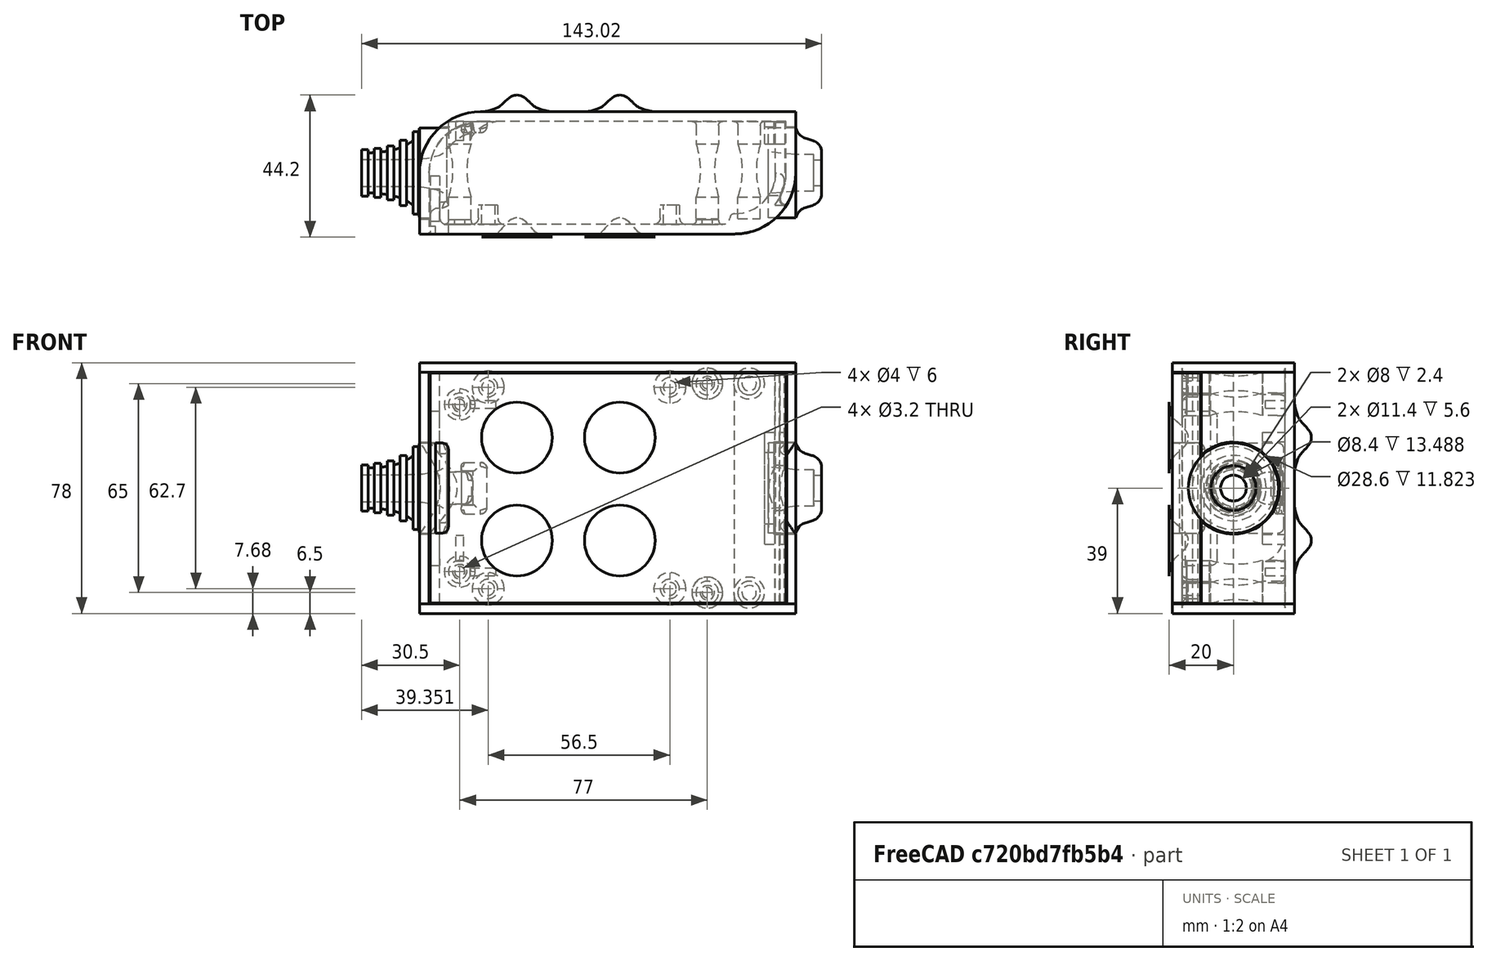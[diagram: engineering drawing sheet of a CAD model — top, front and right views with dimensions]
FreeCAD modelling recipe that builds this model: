
FCSTD DOCUMENT  (FreeCAD 0.19R0.19.2)
Label: enclosure_072
License: All rights reserved
LicenseURL: http://en.wikipedia.org/wiki/All_rights_reserved
objects: Part::MultiFuse×44, Part::Feature×44, Part::Revolution×44, Part::Fillet×22, Part::Cylinder×22, Sketcher::SketchObject×20, Part::Cut×14, Part::Extrusion×13, Part::Box×10, App::MeasureDistance×3
note: 233 computed .brp shape members not serialized (recipe doc carries the construction recipe); baked Part::Feature solids carry a one-line shape summary decoded from their .brp

FEATURE [Sketcher::SketchObject] Sketch  label="topSketch"
  FullyConstrained = true
  sketch-geometry (13):
    g0: LineSegment StartX=117 StartY=19 StartZ=0 EndX=117 EndY=38 EndZ=0
    g1: ArcOfCircle CenterX=98 CenterY=19 CenterZ=0 NormalX=0 NormalY=0 NormalZ=1 AngleXU=0 Radius=19 StartAngle=5.7297 EndAngle=6.28319
    g2: LineSegment StartX=0 StartY=3 StartZ=0 EndX=0 EndY=19 EndZ=0
    g3: LineSegment StartX=19 StartY=38 StartZ=0 EndX=117 EndY=38 EndZ=0
    g4: ArcOfCircle CenterX=19 CenterY=19 CenterZ=0 NormalX=0 NormalY=0 NormalZ=1 AngleXU=0 Radius=19 StartAngle=1.5708 EndAngle=3.14159
    g5: ArcOfCircle CenterX=19 CenterY=19 CenterZ=0 NormalX=0 NormalY=0 NormalZ=1 AngleXU=0 Radius=16 StartAngle=1.5708 EndAngle=3.14159
    g6: ArcOfCircle CenterX=98 CenterY=19 CenterZ=0 NormalX=0 NormalY=0 NormalZ=1 AngleXU=0 Radius=16 StartAngle=5.60905 EndAngle=6.28319
    g7: LineSegment StartX=114 StartY=19 StartZ=0 EndX=114 EndY=35 EndZ=0
    g8: LineSegment StartX=110.5 StartY=9.01251 StartZ=0 EndX=114.163 EndY=9.01251 EndZ=0
    g9: LineSegment StartX=114 StartY=35 StartZ=0 EndX=19 EndY=35 EndZ=0
    g10: LineSegment StartX=0 StartY=3 StartZ=0 EndX=0 EndY=0 EndZ=0
    g11: LineSegment StartX=3 StartY=0 StartZ=0 EndX=0 EndY=0 EndZ=0
    g12: LineSegment StartX=3 StartY=19 StartZ=0 EndX=3 EndY=0 EndZ=0
  constraints (33):
    c: Vertical(g0)
    c: Distance(g0) = 19
    c: Block(g0)
    c: Coincident(g1,g0)
    c: Block(g1)
    c: Vertical(g2)
    c: Block(g2)
    c: Coincident(g3,g0)
    c: Horizontal(g3)
    c: Distance(g3) = 98
    c: Coincident(g4,g3)
    c: Coincident(g4,g2)
    c: Block(g4)
    c: Coincident(g5,g4)
    c: Coincident(g6,g1)
    c: Block(g6)
    c: Block(g5)
    c: Coincident(g7,g6)
    c: Vertical(g7)
    c: Coincident(g8,g6)
    c: Coincident(g8,g1)
    c: Coincident(g9,g7)
    c: Coincident(g9,g5)
    c: Horizontal(g9)
    c: Tangent(g9,g5)
    c: Coincident(g10,g2)
    c: Distance(g10) = 3
    c: Vertical(g10)
    c: Coincident(g11,g10)
    c: Horizontal(g11)
    c: Coincident(g12,g5)
    c: Coincident(g12,g11)
    c: Vertical(g12)
FEATURE [Sketcher::SketchObject] Sketch001  label="bottomSketch"
  FullyConstrained = true
  sketch-geometry (32):
    g0: LineSegment StartX=3.3 StartY=-6.03275e-07 StartZ=0 EndX=98 EndY=-6.03275e-07 EndZ=0
    g1: ArcOfCircle CenterX=98 CenterY=19 CenterZ=0 NormalX=0 NormalY=0 NormalZ=1 AngleXU=0 Radius=19 StartAngle=4.71239 EndAngle=5.71103
    g2: LineSegment StartX=6.3 StartY=8 StartZ=0 EndX=3.3 EndY=8 EndZ=0
    g3: LineSegment StartX=3.3 StartY=8 StartZ=0 EndX=3.3 EndY=-6.03275e-07 EndZ=0
    g4: ArcOfCircle CenterX=8.3 CenterY=5 CenterZ=0 NormalX=0 NormalY=0 NormalZ=1 AngleXU=0 Radius=2 StartAngle=3.14159 EndAngle=4.71239
    g5: LineSegment StartX=6.3 StartY=8 StartZ=0 EndX=6.3 EndY=5 EndZ=0
    g6: ArcOfCircle CenterX=98 CenterY=19 CenterZ=0 NormalX=0 NormalY=0 NormalZ=1 AngleXU=0 Radius=12.7 StartAngle=4.71239 EndAngle=6.28319
    g7: LineSegment StartX=94.7 StartY=3 StartZ=0 EndX=8.3 EndY=3 EndZ=0
    g8-g12: Circle x5 (B-spline internal-alignment scaffolding for g13; pole/knot coordinates omitted)
    g13: BSplineCurve PolesCount=5 KnotsCount=3 Degree=3 IsPeriodic=0
    g14: GeomPoint X=98 Y=6.3 Z=0
    g15: GeomPoint X=96.3938 Y=4.71946 Z=0
    g16: GeomPoint X=94.7 Y=3 Z=0
    g17-g23: Circle x7 (B-spline internal-alignment scaffolding for g24; pole/knot coordinates omitted)
    g24: BSplineCurve PolesCount=7 KnotsCount=5 Degree=3 IsPeriodic=0
    g25-g29: GeomPoint x5 (B-spline internal-alignment scaffolding for g24; pole/knot coordinates omitted)
    g30: ArcOfCircle CenterX=98 CenterY=19 CenterZ=0 NormalX=0 NormalY=0 NormalZ=1 AngleXU=0 Radius=15.7 StartAngle=5.81226 EndAngle=6.28319
    g31: LineSegment StartX=110.7 StartY=19 StartZ=0 EndX=113.7 EndY=19 EndZ=0
  constraints (41):
    c: Horizontal(g0)
    c: Coincident(g1,g0)
    c: Block(g1)
    c: Horizontal(g2)
    c: Distance(g2) = 3
    c: Coincident(g3,g2)
    c: Vertical(g3)
    c: Coincident(g3,g0)
    c: Block(g4)
    c: Block(g2)
    c: Coincident(g5,g2)
    c: Coincident(g5,g4)
    c: Vertical(g5)
    c: Coincident(g6,g1)
    c: Block(g6)
    c: Coincident(g7,g4)
    c: Horizontal(g7)
    c: Block(g0)
    c: Block(g7)
    c: Block(g3)
    c: Coincident(g13,g6)
    c: Weight(g8) = 1
    c: Equal(g8, g9-g12) x4
    c: Coincident(g13,g7)
    c: InternalAlignment(g8-g12 -> g13) x5
    c: InternalAlignment(g14,g13)
    c: InternalAlignment(g15,g13)
    c: InternalAlignment(g16,g13)
    c: Block(g13)
    c: Weight(g17) = 1
    c: Equal(g17, g18-g23) x6
    c: Coincident(g24,g1)
    c: InternalAlignment(g17-g23 -> g24) x7
    c: InternalAlignment(g25-g29 -> g24) x5
    c: Block(g24)
    c: Coincident(g30,g24)
    c: Coincident(g31,g6)
    c: Coincident(g31,g30)
    c: Horizontal(g31)
    c: Block(g31)
    c: Block(g30)
FEATURE [Part::Extrusion] Extrude  label="top"
  Base = -> Sketch
  Dir = (0,0,1)
  DirMode = 2
  FaceMakerClass = Part::FaceMakerBullseye
  LengthFwd = 72
  LengthRev = 0
  Solid = true
  Symmetric = false
FEATURE [Part::Extrusion] Extrude001  label="bottom"
  Base = -> Sketch001
  Dir = (0,0,1)
  DirMode = 2
  FaceMakerClass = Part::FaceMakerBullseye
  LengthFwd = 71.4
  LengthRev = 0
  Placement = pos=(0,0,0.3) rot=(0,0,1;0rad)
  Solid = true
  Symmetric = false
FEATURE [Sketcher::SketchObject] Sketch002  label="topSketch001"
  FullyConstrained = true
  sketch-geometry (6):
    g0: LineSegment StartX=19 StartY=38 StartZ=0 EndX=117 EndY=38 EndZ=0
    g1: ArcOfCircle CenterX=19 CenterY=19 CenterZ=0 NormalX=0 NormalY=0 NormalZ=1 AngleXU=0 Radius=19 StartAngle=1.5708 EndAngle=3.14159
    g2: LineSegment StartX=117 StartY=38 StartZ=0 EndX=117 EndY=19 EndZ=0
    g3: LineSegment StartX=98 StartY=1.0161e-12 StartZ=0 EndX=5.22862e-06 EndY=1.0161e-12 EndZ=0
    g4: LineSegment StartX=5.22862e-06 StartY=19 StartZ=0 EndX=5.22862e-06 EndY=1.0161e-12 EndZ=0
    g5: ArcOfCircle CenterX=98 CenterY=19 CenterZ=0 NormalX=0 NormalY=0 NormalZ=1 AngleXU=0 Radius=19 StartAngle=4.71239 EndAngle=6.28319
  constraints (16):
    c: Horizontal(g0)
    c: Distance(g0) = 98
    c: Coincident(g1,g0)
    c: Block(g1)
    c: Coincident(g2,g0)
    c: Vertical(g2)
    c: Distance(g2) = 19
    c: Horizontal(g3)
    c: Coincident(g4,g1)
    c: Vertical(g4)
    c: Coincident(g3,g4)
    c: Block(g3)
    c: Coincident(g5,g2)
    c: Coincident(g5,g3)
    c: Block(g0)
    c: Block(g5)
FEATURE [Part::Extrusion] Extrude002  label="sideA"
  Base = -> Sketch002
  Dir = (0,0,1)
  DirMode = 2
  FaceMakerClass = Part::FaceMakerBullseye
  LengthFwd = 3
  LengthRev = 0
  Placement = pos=(0,0,-3) rot=(0,0,1;0rad)
  Solid = true
  Symmetric = false
FEATURE [Sketcher::SketchObject] Sketch003  label="topSketch002"
  FullyConstrained = true
  sketch-geometry (6):
    g0: LineSegment StartX=19 StartY=38 StartZ=0 EndX=117 EndY=38 EndZ=0
    g1: ArcOfCircle CenterX=19 CenterY=19 CenterZ=0 NormalX=0 NormalY=0 NormalZ=1 AngleXU=0 Radius=19 StartAngle=1.5708 EndAngle=3.14159
    g2: LineSegment StartX=117 StartY=38 StartZ=0 EndX=117 EndY=19 EndZ=0
    g3: LineSegment StartX=98 StartY=1.0161e-12 StartZ=0 EndX=5.22862e-06 EndY=1.0161e-12 EndZ=0
    g4: LineSegment StartX=5.22862e-06 StartY=19 StartZ=0 EndX=5.22862e-06 EndY=1.0161e-12 EndZ=0
    g5: ArcOfCircle CenterX=98 CenterY=19 CenterZ=0 NormalX=0 NormalY=0 NormalZ=1 AngleXU=0 Radius=19 StartAngle=4.71239 EndAngle=6.28319
  constraints (16):
    c: Horizontal(g0)
    c: Distance(g0) = 98
    c: Coincident(g1,g0)
    c: Block(g1)
    c: Coincident(g2,g0)
    c: Vertical(g2)
    c: Distance(g2) = 19
    c: Horizontal(g3)
    c: Coincident(g4,g1)
    c: Vertical(g4)
    c: Coincident(g3,g4)
    c: Block(g3)
    c: Coincident(g5,g2)
    c: Coincident(g5,g3)
    c: Block(g0)
    c: Block(g5)
FEATURE [Part::Extrusion] Extrude003  label="sideB"
  Base = -> Sketch003
  Dir = (0,0,1)
  DirMode = 2
  FaceMakerClass = Part::FaceMakerBullseye
  LengthFwd = 3
  LengthRev = 0
  Placement = pos=(0,0,72) rot=(0,0,1;0rad)
  Solid = true
  Symmetric = false
FEATURE [Sketcher::SketchObject] Sketch004
  FullyConstrained = true
  MapMode = 3
  Placement = pos=(0,0,0) rot=(1,0,0;1.5708rad)
  Support = -> [Extrude]
  sketch-geometry (8):
    g0: Circle CenterX=80.351 CenterY=-67.6202 CenterZ=0 NormalX=0 NormalY=0 NormalZ=1 AngleXU=0 Radius=2
    g1: Circle CenterX=80.351 CenterY=-67.6202 CenterZ=0 NormalX=0 NormalY=0 NormalZ=1 AngleXU=0 Radius=3
    g2: Circle CenterX=80.351 CenterY=-4.92017 CenterZ=0 NormalX=0 NormalY=0 NormalZ=1 AngleXU=0 Radius=2
    g3: Circle CenterX=80.351 CenterY=-4.92017 CenterZ=0 NormalX=0 NormalY=0 NormalZ=1 AngleXU=0 Radius=3
    g4: Circle CenterX=23.851 CenterY=-4.92017 CenterZ=0 NormalX=0 NormalY=0 NormalZ=1 AngleXU=0 Radius=2
    g5: Circle CenterX=23.851 CenterY=-4.92017 CenterZ=0 NormalX=0 NormalY=0 NormalZ=1 AngleXU=0 Radius=3
    g6: Circle CenterX=23.851 CenterY=-67.6202 CenterZ=0 NormalX=0 NormalY=0 NormalZ=1 AngleXU=0 Radius=2
    g7: Circle CenterX=23.851 CenterY=-67.6202 CenterZ=0 NormalX=0 NormalY=0 NormalZ=1 AngleXU=0 Radius=3
  constraints (8):
    c: Block(g3)
    c: Block(g2)
    c: Block(g1)
    c: Block(g0)
    c: Block(g6)
    c: Block(g7)
    c: Block(g4)
    c: Block(g5)
FEATURE [Part::Extrusion] Extrude004
  Base = -> Sketch004
  Dir = (0,-1,2e-16)
  DirMode = 2
  FaceMakerClass = Part::FaceMakerBullseye
  LengthFwd = 6
  LengthRev = 0
  Placement = pos=(0,9,0) rot=(0,0,1;0rad)
  Solid = true
  Symmetric = false
FEATURE [Sketcher::SketchObject] Sketch005
  FullyConstrained = true
  MapMode = 3
  Placement = pos=(0,0,0) rot=(1,0,0;1.5708rad)
  Support = -> [Extrude]
  sketch-geometry (8):
    g0: Circle CenterX=80.351 CenterY=-67.6202 CenterZ=0 NormalX=0 NormalY=0 NormalZ=1 AngleXU=0 Radius=3
    g1: Circle CenterX=80.351 CenterY=-4.92017 CenterZ=0 NormalX=0 NormalY=0 NormalZ=1 AngleXU=0 Radius=3
    g2: Circle CenterX=23.851 CenterY=-4.92017 CenterZ=0 NormalX=0 NormalY=0 NormalZ=1 AngleXU=0 Radius=3
    g3: Circle CenterX=23.851 CenterY=-67.6202 CenterZ=0 NormalX=0 NormalY=0 NormalZ=1 AngleXU=0 Radius=3
    g4: Circle CenterX=23.851 CenterY=-67.6202 CenterZ=0 NormalX=0 NormalY=0 NormalZ=1 AngleXU=0 Radius=5
    g5: Circle CenterX=80.351 CenterY=-67.6202 CenterZ=0 NormalX=0 NormalY=0 NormalZ=1 AngleXU=0 Radius=5
    g6: Circle CenterX=23.851 CenterY=-4.92017 CenterZ=0 NormalX=0 NormalY=0 NormalZ=1 AngleXU=0 Radius=5
    g7: Circle CenterX=80.351 CenterY=-4.92017 CenterZ=0 NormalX=0 NormalY=0 NormalZ=1 AngleXU=0 Radius=5
  constraints (8):
    c: Block(g1)
    c: Block(g0)
    c: Block(g3)
    c: Block(g2)
    c: Block(g5)
    c: Block(g4)
    c: Block(g6)
    c: Block(g7)
FEATURE [Part::Extrusion] Extrude005
  Base = -> Sketch005
  Dir = (0,-1,2e-16)
  DirMode = 2
  FaceMakerClass = Part::FaceMakerBullseye
  LengthFwd = 2
  LengthRev = 0
  Solid = true
  Symmetric = false
FEATURE [Sketcher::SketchObject] Sketch006
  FullyConstrained = true
  MapMode = 3
  Placement = pos=(0,0,0) rot=(1,0,0;1.5708rad)
  sketch-geometry (8):
    g0: Circle CenterX=80.351 CenterY=-67.6202 CenterZ=0 NormalX=0 NormalY=0 NormalZ=1 AngleXU=0 Radius=3
    g1: Circle CenterX=80.351 CenterY=-4.92017 CenterZ=0 NormalX=0 NormalY=0 NormalZ=1 AngleXU=0 Radius=3
    g2: Circle CenterX=23.851 CenterY=-4.92017 CenterZ=0 NormalX=0 NormalY=0 NormalZ=1 AngleXU=0 Radius=3
    g3: Circle CenterX=23.851 CenterY=-67.6202 CenterZ=0 NormalX=0 NormalY=0 NormalZ=1 AngleXU=0 Radius=3
    g4: Circle CenterX=23.851 CenterY=-67.6202 CenterZ=0 NormalX=0 NormalY=0 NormalZ=1 AngleXU=0 Radius=5
    g5: Circle CenterX=80.351 CenterY=-67.6202 CenterZ=0 NormalX=0 NormalY=0 NormalZ=1 AngleXU=0 Radius=5
    g6: Circle CenterX=23.851 CenterY=-4.92017 CenterZ=0 NormalX=0 NormalY=0 NormalZ=1 AngleXU=0 Radius=5
    g7: Circle CenterX=80.351 CenterY=-4.92017 CenterZ=0 NormalX=0 NormalY=0 NormalZ=1 AngleXU=0 Radius=5
  constraints (8):
    c: Block(g1)
    c: Block(g0)
    c: Block(g3)
    c: Block(g2)
    c: Block(g5)
    c: Block(g4)
    c: Block(g6)
    c: Block(g7)
FEATURE [Part::Extrusion] Extrude007
  Base = -> Sketch006
  Dir = (0,-1,2e-16)
  DirMode = 2
  FaceMakerClass = Part::FaceMakerBullseye
  LengthFwd = 2
  LengthRev = 0
  Solid = true
  Symmetric = false
FEATURE [Part::Fillet] Fillet
  Base = -> Extrude007
  Edges = 4 edges r=1.99: [Edge6,Edge12,Edge18,Edge24]
FEATURE [Part::Cut] Cut
  Base = -> Extrude005
  Placement = pos=(0,5,0) rot=(0,0,1;0rad)
  Tool = -> Fillet
FEATURE [Part::MultiFuse] Fusion  label="pCBScrews"
  Placement = pos=(-2.5,0,72.3) rot=(0,0,1;0rad)
  Shapes = -> [Extrude004,Cut]
FEATURE [App::MeasureDistance] Distance  label="Distance: 0.69 mm"
  Distance = 0.685967
  P1 = (24.0138,2.9647,0.3)
  P2 = (23.8901,3,-0.373787)
FEATURE [App::MeasureDistance] Distance001  label="Distance: 0.53 mm"
  Distance = 0.533607
  P1 = (80.2939,3,72.2334)
  P2 = (80.281,2.99661,71.7)
FEATURE [Part::Fillet] Fillet001
  Base = -> Extrude001
  Edges = 1 edges r=2.4: [Edge17]
FEATURE [Part::Fillet] Fillet002  label="bottom001"
  Base = -> Fillet001
  Edges = 1 edges r=2.4: [Edge36]
FEATURE [Part::Fillet] Fillet003  label="top001"
  Base = -> Extrude
  Edges = 1 edges r=2: [Edge1]
FEATURE [Sketcher::SketchObject] Sketch007
  FullyConstrained = true
  sketch-geometry (16):
    g0: LineSegment StartX=4 StartY=0 StartZ=0 EndX=4 EndY=2.4 EndZ=0
    g1: LineSegment StartX=4 StartY=2.4 StartZ=0 EndX=7 EndY=2.4 EndZ=0
    g2: LineSegment StartX=4 StartY=0 StartZ=0 EndX=5.7 EndY=0 EndZ=0
    g3: LineSegment StartX=5.7 StartY=0 StartZ=0 EndX=5.7 EndY=-5.6 EndZ=0
    g4-g8: Circle x5 (B-spline internal-alignment scaffolding for g9; pole/knot coordinates omitted)
    g9: BSplineCurve PolesCount=5 KnotsCount=3 Degree=3 IsPeriodic=0
    g10: GeomPoint X=7 Y=2.4 Z=0
    g11: GeomPoint X=10.4582 Y=-1.55472 Z=0
    g12: GeomPoint X=14 Y=-5.6 Z=0
    g13: LineSegment StartX=14 StartY=-5.6 StartZ=0 EndX=14 EndY=-14.1 EndZ=0
    g14: LineSegment StartX=14 StartY=-14.1 StartZ=0 EndX=6.5 EndY=-14.1 EndZ=0
    g15: LineSegment StartX=5.7 StartY=-5.6 StartZ=0 EndX=6.5 EndY=-14.1 EndZ=0
  constraints (28):
    c: Distance(g0) = 2.4
    c: Vertical(g0)
    c: Block(g0)
    c: Coincident(g1,g0)
    c: Horizontal(g1)
    c: Distance(g1) = 3
    c: Coincident(g2,g0)
    c: Horizontal(g2)
    c: Distance(g2) = 1.7
    c: Coincident(g3,g2)
    c: Vertical(g3)
    c: Distance(g3) = 5.6
    c: Coincident(g9,g1)
    c: Weight(g4) = 1
    c: Equal(g4, g5-g8) x4
    c: InternalAlignment(g4-g8 -> g9) x5
    c: InternalAlignment(g10,g9)
    c: InternalAlignment(g11,g9)
    c: InternalAlignment(g12,g9)
    c: Block(g9)
    c: Coincident(g13,g9)
    c: Vertical(g13)
    c: Distance(g13) = 8.5
    c: Coincident(g14,g13)
    c: Horizontal(g14)
    c: Distance(g14) = 7.5
    c: Coincident(g15,g3)
    c: Coincident(g15,g14)
FEATURE [Part::Feature] Face
  shape: bbox 10 x 16.5 x 2e-07 mm, 1 faces, 0 solids (baked)
FEATURE [Part::Revolution] Revolve  label="plugHousing"
  Angle = 360
  Axis = (0,1,0)
  Base = (0,0,0)
  FaceMakerClass = Part::FaceMakerBullseye
  Placement = pos=(0,0,36.15) rot=(0,0,1;0rad)
  Solid = false
  Source = -> Face
  Symmetric = false
FEATURE [Part::Feature] Face001
  shape: bbox 10 x 16.5 x 2e-07 mm, 1 faces, 0 solids (baked)
FEATURE [Part::Revolution] Revolve001  label="plugHousing001"
  Angle = 360
  Axis = (0,1,0)
  Base = (0,0,0)
  FaceMakerClass = Part::FaceMakerBullseye
  Placement = pos=(0,0,36.15) rot=(0,0,1;0rad)
  Solid = false
  Source = -> Face001
  Symmetric = false
FEATURE [Part::MultiFuse] Fusion001  label="plugHousing002"
  Placement = pos=(0,0,0) rot=(0,0,1;1.5708rad)
  Shapes = -> [Revolve001,Revolve]
FEATURE [Part::Feature] Face002
  shape: bbox 10 x 16.5 x 2e-07 mm, 1 faces, 0 solids (baked)
FEATURE [Part::Revolution] Revolve003  label="plugHousing005"
  Angle = 360
  Axis = (0,1,0)
  Base = (0,0,0)
  FaceMakerClass = Part::FaceMakerBullseye
  Placement = pos=(0,0,36.15) rot=(0,0,1;0rad)
  Solid = false
  Source = -> Face002
  Symmetric = false
FEATURE [Part::Feature] Face003
  shape: bbox 10 x 16.5 x 2e-07 mm, 1 faces, 0 solids (baked)
FEATURE [Part::Revolution] Revolve002  label="plugHousing003"
  Angle = 360
  Axis = (0,1,0)
  Base = (0,0,0)
  FaceMakerClass = Part::FaceMakerBullseye
  Placement = pos=(0,0,36.15) rot=(0,0,1;0rad)
  Solid = false
  Source = -> Face003
  Symmetric = false
FEATURE [Part::MultiFuse] Fusion002  label="plugHousing004"
  Placement = pos=(0,0,0) rot=(0,0,1;1.5708rad)
  Shapes = -> [Revolve002,Revolve003]
FEATURE [Part::MultiFuse] Fusion003  label="plugHousing006"
  Placement = pos=(0,19,0) rot=(0,0,1;3.14159rad)
  Shapes = -> [Fusion002,Fusion001]
FEATURE [Part::Feature] Face004
  shape: bbox 10 x 16.5 x 2e-07 mm, 1 faces, 0 solids (baked)
FEATURE [Part::Revolution] Revolve006  label="plugHousing010"
  Angle = 360
  Axis = (0,1,0)
  Base = (0,0,0)
  FaceMakerClass = Part::FaceMakerBullseye
  Placement = pos=(0,0,36.15) rot=(0,0,1;0rad)
  Solid = false
  Source = -> Face004
  Symmetric = false
FEATURE [Part::Feature] Face005
  shape: bbox 10 x 16.5 x 2e-07 mm, 1 faces, 0 solids (baked)
FEATURE [Part::Revolution] Revolve007  label="plugHousing011"
  Angle = 360
  Axis = (0,1,0)
  Base = (0,0,0)
  FaceMakerClass = Part::FaceMakerBullseye
  Placement = pos=(0,0,36.15) rot=(0,0,1;0rad)
  Solid = false
  Source = -> Face005
  Symmetric = false
FEATURE [Part::Feature] Face006
  shape: bbox 10 x 16.5 x 2e-07 mm, 1 faces, 0 solids (baked)
FEATURE [Part::Revolution] Revolve004  label="plugHousing007"
  Angle = 360
  Axis = (0,1,0)
  Base = (0,0,0)
  FaceMakerClass = Part::FaceMakerBullseye
  Placement = pos=(0,0,36.15) rot=(0,0,1;0rad)
  Solid = false
  Source = -> Face006
  Symmetric = false
FEATURE [Part::MultiFuse] Fusion004  label="plugHousing009"
  Placement = pos=(0,0,0) rot=(0,0,1;1.5708rad)
  Shapes = -> [Revolve004,Revolve007]
FEATURE [Part::Feature] Face007
  shape: bbox 10 x 16.5 x 2e-07 mm, 1 faces, 0 solids (baked)
FEATURE [Part::Revolution] Revolve005  label="plugHousing008"
  Angle = 360
  Axis = (0,1,0)
  Base = (0,0,0)
  FaceMakerClass = Part::FaceMakerBullseye
  Placement = pos=(0,0,36.15) rot=(0,0,1;0rad)
  Solid = false
  Source = -> Face007
  Symmetric = false
FEATURE [Part::MultiFuse] Fusion005  label="plugHousing012"
  Placement = pos=(0,0,0) rot=(0,0,1;1.5708rad)
  Shapes = -> [Revolve006,Revolve005]
FEATURE [Part::MultiFuse] Fusion006  label="plugHousing013"
  Placement = pos=(0,19,0) rot=(0,0,1;3.14159rad)
  Shapes = -> [Fusion005,Fusion004]
FEATURE [Part::MultiFuse] Fusion007  label="plugHousing014"
  Placement = pos=(122.621,0,-0.15) rot=(0,0,1;0rad)
  Shapes = -> [Fusion003,Fusion006]
FEATURE [Part::Cylinder] Cylinder002
  Angle = 360
  AttacherType = Attacher::AttachEngine3D
  Height = 20
  Placement = pos=(0,0,36.15) rot=(0,0,1;0rad)
  Radius = 4
FEATURE [Part::Cylinder] Cylinder003
  Angle = 360
  AttacherType = Attacher::AttachEngine3D
  Height = 10
  Placement = pos=(0,0,36.15) rot=(0,0,1;0rad)
  Radius = 4
FEATURE [Part::MultiFuse] Fusion009  label="removeToCreateHoleForPlugHousing"
  Placement = pos=(70,19,36.15) rot=(0,1,0;1.5708rad)
  Shapes = -> [Cylinder002,Cylinder003]
FEATURE [Part::Cylinder] Cylinder004
  Angle = 360
  AttacherType = Attacher::AttachEngine3D
  Height = 20
  Placement = pos=(0,0,36.15) rot=(0,0,1;0rad)
  Radius = 4
FEATURE [Part::Cylinder] Cylinder005
  Angle = 360
  AttacherType = Attacher::AttachEngine3D
  Height = 10
  Placement = pos=(0,0,36.15) rot=(0,0,1;0rad)
  Radius = 4
FEATURE [Part::MultiFuse] Fusion010  label="removeToCreateHoleForPlugHousing001"
  Placement = pos=(70,19,36.15) rot=(0,1,0;1.5708rad)
  Shapes = -> [Cylinder004,Cylinder005]
FEATURE [Part::Cut] Cut001
  Base = -> Fillet003
  Tool = -> Fusion010
FEATURE [Part::Cut] Cut002  label="Bottom"
  Base = -> Fillet002
  Tool = -> Fusion009
FEATURE [Part::Feature] Face008
  shape: bbox 10 x 16.5 x 2e-07 mm, 1 faces, 0 solids (baked)
FEATURE [Part::Revolution] Revolve011  label="plugHousing021"
  Angle = 360
  Axis = (0,1,0)
  Base = (0,0,0)
  FaceMakerClass = Part::FaceMakerBullseye
  Placement = pos=(0,0,36.15) rot=(0,0,1;0rad)
  Solid = false
  Source = -> Face008
  Symmetric = false
FEATURE [Part::Feature] Face009
  shape: bbox 10 x 16.5 x 2e-07 mm, 1 faces, 0 solids (baked)
FEATURE [Part::Revolution] Revolve012  label="plugHousing022"
  Angle = 360
  Axis = (0,1,0)
  Base = (0,0,0)
  FaceMakerClass = Part::FaceMakerBullseye
  Placement = pos=(0,0,36.15) rot=(0,0,1;0rad)
  Solid = false
  Source = -> Face009
  Symmetric = false
FEATURE [Part::Feature] Face010
  shape: bbox 10 x 16.5 x 2e-07 mm, 1 faces, 0 solids (baked)
FEATURE [Part::Feature] Face011
  shape: bbox 10 x 16.5 x 2e-07 mm, 1 faces, 0 solids (baked)
FEATURE [Part::Revolution] Revolve014  label="plugHousing026"
  Angle = 360
  Axis = (0,1,0)
  Base = (0,0,0)
  FaceMakerClass = Part::FaceMakerBullseye
  Placement = pos=(0,0,36.15) rot=(0,0,1;0rad)
  Solid = false
  Source = -> Face011
  Symmetric = false
FEATURE [Part::Feature] Face012
  shape: bbox 10 x 16.5 x 2e-07 mm, 1 faces, 0 solids (baked)
FEATURE [Part::Revolution] Revolve009  label="plugHousing016"
  Angle = 360
  Axis = (0,1,0)
  Base = (0,0,0)
  FaceMakerClass = Part::FaceMakerBullseye
  Placement = pos=(0,0,36.15) rot=(0,0,1;0rad)
  Solid = false
  Source = -> Face012
  Symmetric = false
FEATURE [Part::Feature] Face013
  shape: bbox 10 x 16.5 x 2e-07 mm, 1 faces, 0 solids (baked)
FEATURE [Part::Revolution] Revolve015  label="plugHousing027"
  Angle = 360
  Axis = (0,1,0)
  Base = (0,0,0)
  FaceMakerClass = Part::FaceMakerBullseye
  Placement = pos=(0,0,36.15) rot=(0,0,1;0rad)
  Solid = false
  Source = -> Face013
  Symmetric = false
FEATURE [Part::Feature] Face014
  shape: bbox 10 x 16.5 x 2e-07 mm, 1 faces, 0 solids (baked)
FEATURE [Part::Revolution] Revolve010  label="plugHousing017"
  Angle = 360
  Axis = (0,1,0)
  Base = (0,0,0)
  FaceMakerClass = Part::FaceMakerBullseye
  Placement = pos=(0,0,36.15) rot=(0,0,1;0rad)
  Solid = false
  Source = -> Face014
  Symmetric = false
FEATURE [Part::MultiFuse] Fusion015  label="plugHousing024"
  Placement = pos=(0,0,0) rot=(0,0,1;1.5708rad)
  Shapes = -> [Revolve010,Revolve015]
FEATURE [Part::Feature] Face015
  shape: bbox 10 x 16.5 x 2e-07 mm, 1 faces, 0 solids (baked)
FEATURE [Part::Revolution] Revolve013  label="plugHousing025"
  Angle = 360
  Axis = (0,1,0)
  Base = (0,0,0)
  FaceMakerClass = Part::FaceMakerBullseye
  Placement = pos=(0,0,36.15) rot=(0,0,1;0rad)
  Solid = false
  Source = -> Face015
  Symmetric = false
FEATURE [Part::MultiFuse] Fusion011  label="plugHousing018"
  Placement = pos=(0,0,0) rot=(0,0,1;1.5708rad)
  Shapes = -> [Revolve014,Revolve013]
FEATURE [Part::MultiFuse] Fusion012  label="plugHousing019"
  Placement = pos=(0,19,0) rot=(0,0,1;3.14159rad)
  Shapes = -> [Fusion011,Fusion015]
FEATURE [Part::Feature] Face016
  shape: bbox 10 x 16.5 x 2e-07 mm, 1 faces, 0 solids (baked)
FEATURE [Part::Revolution] Revolve019  label="plugHousing033"
  Angle = 360
  Axis = (0,1,0)
  Base = (0,0,0)
  FaceMakerClass = Part::FaceMakerBullseye
  Placement = pos=(0,0,36.15) rot=(0,0,1;0rad)
  Solid = false
  Source = -> Face016
  Symmetric = false
FEATURE [Part::Feature] Face017
  shape: bbox 10 x 16.5 x 2e-07 mm, 1 faces, 0 solids (baked)
FEATURE [Part::Revolution] Revolve020  label="plugHousing034"
  Angle = 360
  Axis = (0,1,0)
  Base = (0,0,0)
  FaceMakerClass = Part::FaceMakerBullseye
  Placement = pos=(0,0,36.15) rot=(0,0,1;0rad)
  Solid = false
  Source = -> Face017
  Symmetric = false
FEATURE [Part::Feature] Face018
  shape: bbox 10 x 16.5 x 2e-07 mm, 1 faces, 0 solids (baked)
FEATURE [Part::Revolution] Revolve016  label="plugHousing030"
  Angle = 360
  Axis = (0,1,0)
  Base = (0,0,0)
  FaceMakerClass = Part::FaceMakerBullseye
  Placement = pos=(0,0,36.15) rot=(0,0,1;0rad)
  Solid = false
  Source = -> Face018
  Symmetric = false
FEATURE [Part::MultiFuse] Fusion020  label="plugHousing038"
  Placement = pos=(0,0,0) rot=(0,0,1;1.5708rad)
  Shapes = -> [Revolve016,Revolve020]
FEATURE [Part::Feature] Face019
  shape: bbox 10 x 16.5 x 2e-07 mm, 1 faces, 0 solids (baked)
FEATURE [Part::Feature] Face020
  shape: bbox 10 x 16.5 x 2e-07 mm, 1 faces, 0 solids (baked)
FEATURE [Part::Revolution] Revolve017  label="plugHousing031"
  Angle = 360
  Axis = (0,1,0)
  Base = (0,0,0)
  FaceMakerClass = Part::FaceMakerBullseye
  Placement = pos=(0,0,36.15) rot=(0,0,1;0rad)
  Solid = false
  Source = -> Face020
  Symmetric = false
FEATURE [Part::MultiFuse] Fusion021  label="plugHousing039"
  Placement = pos=(0,0,0) rot=(0,0,1;1.5708rad)
  Shapes = -> [Revolve019,Revolve017]
FEATURE [Part::MultiFuse] Fusion023  label="plugHousing041"
  Placement = pos=(0,19,0) rot=(0,0,1;3.14159rad)
  Shapes = -> [Fusion021,Fusion020]
FEATURE [Part::Revolution] Revolve022  label="plugHousing043"
  Angle = 360
  Axis = (0,1,0)
  Base = (0,0,0)
  FaceMakerClass = Part::FaceMakerBullseye
  Placement = pos=(0,0,36.15) rot=(0,0,1;0rad)
  Solid = false
  Source = -> Face019
  Symmetric = false
FEATURE [Part::Feature] Face021
  shape: bbox 10 x 16.5 x 2e-07 mm, 1 faces, 0 solids (baked)
FEATURE [Part::Revolution] Revolve023  label="plugHousing044"
  Angle = 360
  Axis = (0,1,0)
  Base = (0,0,0)
  FaceMakerClass = Part::FaceMakerBullseye
  Placement = pos=(0,0,36.15) rot=(0,0,1;0rad)
  Solid = false
  Source = -> Face021
  Symmetric = false
FEATURE [Part::Feature] Face022
  shape: bbox 10 x 16.5 x 2e-07 mm, 1 faces, 0 solids (baked)
FEATURE [Part::Revolution] Revolve018  label="plugHousing032"
  Angle = 360
  Axis = (0,1,0)
  Base = (0,0,0)
  FaceMakerClass = Part::FaceMakerBullseye
  Placement = pos=(0,0,36.15) rot=(0,0,1;0rad)
  Solid = false
  Source = -> Face022
  Symmetric = false
FEATURE [Part::MultiFuse] Fusion022  label="plugHousing040"
  Placement = pos=(0,0,0) rot=(0,0,1;1.5708rad)
  Shapes = -> [Revolve018,Revolve023]
FEATURE [Part::Feature] Face023
  shape: bbox 10 x 16.5 x 2e-07 mm, 1 faces, 0 solids (baked)
FEATURE [Part::Revolution] Revolve021  label="plugHousing035"
  Angle = 360
  Axis = (0,1,0)
  Base = (0,0,0)
  FaceMakerClass = Part::FaceMakerBullseye
  Placement = pos=(0,0,36.15) rot=(0,0,1;0rad)
  Solid = false
  Source = -> Face023
  Symmetric = false
FEATURE [Part::MultiFuse] Fusion018  label="plugHousing036"
  Placement = pos=(0,0,0) rot=(0,0,1;1.5708rad)
  Shapes = -> [Revolve022,Revolve021]
FEATURE [Part::MultiFuse] Fusion019  label="plugHousing037"
  Placement = pos=(0,19,0) rot=(0,0,1;3.14159rad)
  Shapes = -> [Fusion018,Fusion022]
FEATURE [Part::MultiFuse] Fusion024  label="plugHousing042"
  Placement = pos=(122.621,0,-0.15) rot=(0,0,1;0rad)
  Shapes = -> [Fusion023,Fusion019]
FEATURE [Part::Cylinder] Cylinder006
  Angle = 360
  AttacherType = Attacher::AttachEngine3D
  Height = 20
  Placement = pos=(0,0,36.15) rot=(0,0,1;0rad)
  Radius = 14.3
FEATURE [Part::Cylinder] Cylinder007
  Angle = 360
  AttacherType = Attacher::AttachEngine3D
  Height = 10
  Placement = pos=(0,0,36.15) rot=(0,0,1;0rad)
  Radius = 4
FEATURE [Part::MultiFuse] Fusion026  label="removeToCreteHoleForPlugHousing"
  Placement = pos=(70,19,36) rot=(0,1,0;1.5708rad)
  Shapes = -> [Cylinder006,Cylinder007]
FEATURE [Part::Box] Box001  label="Cube001"
  AttacherType = Attacher::AttachEngine3D
  Height = 28
  Length = 3
  Placement = pos=(110.7,19,22) rot=(0,0,1;0rad)
  Width = 15.7
FEATURE [Part::Cut] Cut003  label="top002"
  Base = -> Cut001
  Tool = -> Fusion007
FEATURE [Part::Revolution] Revolve008  label="plugHousing015"
  Angle = 360
  Axis = (0,1,0)
  Base = (0,0,0)
  FaceMakerClass = Part::FaceMakerBullseye
  Placement = pos=(0,0,36.15) rot=(0,0,1;0rad)
  Solid = false
  Source = -> Face010
  Symmetric = false
FEATURE [Part::MultiFuse] Fusion014  label="plugHousing023"
  Placement = pos=(0,0,0) rot=(0,0,1;1.5708rad)
  Shapes = -> [Revolve011,Revolve009]
FEATURE [Part::MultiFuse] Fusion013  label="plugHousing020"
  Placement = pos=(0,0,0) rot=(0,0,1;1.5708rad)
  Shapes = -> [Revolve008,Revolve012]
FEATURE [Part::MultiFuse] Fusion016  label="plugHousing028"
  Placement = pos=(0,19,0) rot=(0,0,1;3.14159rad)
  Shapes = -> [Fusion014,Fusion013]
FEATURE [Part::MultiFuse] Fusion017  label="plugHousing029"
  Placement = pos=(122.621,0,-0.15) rot=(0,0,1;0rad)
  Shapes = -> [Fusion016,Fusion012]
FEATURE [Part::Cut] Cut004  label="top003"
  Base = -> Cut003
  Placement = pos=(1,0,0) rot=(0,0,1;0rad)
  Tool = -> Fusion026
FEATURE [Part::Cylinder] Cylinder008
  Angle = 360
  AttacherType = Attacher::AttachEngine3D
  Height = 20
  Placement = pos=(0,0,36.15) rot=(0,0,1;0rad)
  Radius = 10.3
FEATURE [Part::Cylinder] Cylinder009
  Angle = 360
  AttacherType = Attacher::AttachEngine3D
  Height = 10
  Placement = pos=(0,0,36.15) rot=(0,0,1;0rad)
  Radius = 4
FEATURE [Part::MultiFuse] Fusion027  label="removeToCreteHoleForPlugHousing001"
  Placement = pos=(70,19,36) rot=(0,1,0;1.5708rad)
  Shapes = -> [Cylinder008,Cylinder009]
FEATURE [Part::Cut] Cut005  label="plugHousingTab"
  Base = -> Box001
  Tool = -> Fusion027
FEATURE [Part::MultiFuse] Fusion028  label="plugHousing045"
  Shapes = -> [Fusion024,Cut005]
FEATURE [Part::Box] Box002  label="Cube002"
  AttacherType = Attacher::AttachEngine3D
  Height = 28.8
  Length = 3
  Placement = pos=(107.3,28,21.6) rot=(0,0,1;0rad)
  Width = 7
FEATURE [Part::Box] Box003  label="Cube003"
  AttacherType = Attacher::AttachEngine3D
  Height = 3
  Length = 6.4
  Placement = pos=(107.3,28,18.6) rot=(0,0,1;0rad)
  Width = 7
FEATURE [Part::Box] Box004  label="Cube004"
  AttacherType = Attacher::AttachEngine3D
  Height = 3
  Length = 6.4
  Placement = pos=(107.3,28,50.4) rot=(0,0,1;0rad)
  Width = 7
FEATURE [Part::MultiFuse] Fusion029  label="plugHousingBracketHolder"
  Shapes = -> [Box004,Box002,Box003]
FEATURE [Part::Cylinder] Cylinder010
  Angle = 360
  AttacherType = Attacher::AttachEngine3D
  Height = 20
  Placement = pos=(0,0,36.15) rot=(0,0,1;0rad)
  Radius = 14.3
FEATURE [Part::Cylinder] Cylinder011
  Angle = 360
  AttacherType = Attacher::AttachEngine3D
  Height = 10
  Placement = pos=(0,0,36.15) rot=(0,0,1;0rad)
  Radius = 4
FEATURE [Part::MultiFuse] Fusion030  label="removeToCreteHoleForPlugHousing002"
  Placement = pos=(70,19,36) rot=(0,1,0;1.5708rad)
  Shapes = -> [Cylinder010,Cylinder011]
FEATURE [Part::Cut] Cut006  label="plugHousingBracketHolder001"
  Base = -> Fusion029
  Tool = -> Fusion030
FEATURE [Part::Cylinder] Cylinder012
  Angle = 360
  AttacherType = Attacher::AttachEngine3D
  Height = 20
  Placement = pos=(0,0,36.15) rot=(0,0,1;0rad)
  Radius = 7
FEATURE [Part::Cylinder] Cylinder013
  Angle = 360
  AttacherType = Attacher::AttachEngine3D
  Height = 10
  Placement = pos=(0,0,36.15) rot=(0,0,1;0rad)
  Radius = 4
FEATURE [Part::MultiFuse] Fusion032  label="removeToCreteHoleForPlugHousing003"
  Placement = pos=(70,19,36) rot=(0,1,0;1.5708rad)
  Shapes = -> [Cylinder012,Cylinder013]
FEATURE [Part::Cut] Cut007  label="bottom002"
  Base = -> Cut002
  Tool = -> Fusion032
FEATURE [Sketcher::SketchObject] Sketch008
  FullyConstrained = true
  sketch-geometry (54):
    g0: LineSegment StartX=-4.2 StartY=0 StartZ=0 EndX=-6.2 EndY=0 EndZ=0
    g1: LineSegment StartX=-14 StartY=-18 StartZ=0 EndX=-14 EndY=-26.5 EndZ=0
    g2: LineSegment StartX=-4.2 StartY=0 StartZ=0 EndX=-4.2 EndY=-13.4877 EndZ=0
    g3: Circle CenterX=-4.2 CenterY=-13.4877 CenterZ=0 NormalX=0 NormalY=0 NormalZ=1 AngleXU=0 Radius=1
    g4: Circle CenterX=-4.2 CenterY=-26.5 CenterZ=0 NormalX=0 NormalY=0 NormalZ=1 AngleXU=0 Radius=1
    g5: Circle CenterX=-8.2 CenterY=-26.5 CenterZ=0 NormalX=0 NormalY=0 NormalZ=1 AngleXU=0 Radius=1
    g6: BSplineCurve PolesCount=3 KnotsCount=2 Degree=2 IsPeriodic=0
    g7: GeomPoint X=-4.2 Y=-13.4877 Z=0
    g8: GeomPoint X=-8.2 Y=-26.5 Z=0
    g9: LineSegment StartX=-14 StartY=-26.5 StartZ=0 EndX=-8.2 EndY=-26.5 EndZ=0
    g10: LineSegment StartX=-10.15 StartY=-12 StartZ=0 EndX=-10.15 EndY=-14 EndZ=0
    g11: LineSegment StartX=-12.8401 StartY=-16 StartZ=0 EndX=-10.1571 EndY=-16 EndZ=0
    g12: LineSegment StartX=-10.15 StartY=-14 StartZ=0 EndX=-8.70761 EndY=-14 EndZ=0
    g13: LineSegment StartX=-12.8401 StartY=-16 StartZ=0 EndX=-12.8401 EndY=-17.6958 EndZ=0
    g14: LineSegment StartX=-10.15 StartY=-12 StartZ=0 EndX=-7.79258 EndY=-12 EndZ=0
    g15: Circle CenterX=-6.2215 CenterY=-2 CenterZ=0 NormalX=0 NormalY=0 NormalZ=1 AngleXU=0 Radius=1
    g16: Circle CenterX=-6.22762 CenterY=-2.58724 CenterZ=0 NormalX=0 NormalY=0 NormalZ=1 AngleXU=0 Radius=1
    g17: Circle CenterX=-6.32538 CenterY=-4 CenterZ=0 NormalX=0 NormalY=0 NormalZ=1 AngleXU=0 Radius=1
    g18: BSplineCurve PolesCount=3 KnotsCount=2 Degree=2 IsPeriodic=0
    g19: GeomPoint X=-6.2215 Y=-2 Z=0
    g20: GeomPoint X=-6.32538 Y=-4 Z=0
    g21: Circle CenterX=-6.48644 CenterY=-5.99526 CenterZ=0 NormalX=0 NormalY=0 NormalZ=1 AngleXU=0 Radius=1
    g22: Circle CenterX=-6.58486 CenterY=-6.99526 CenterZ=0 NormalX=0 NormalY=0 NormalZ=1 AngleXU=0 Radius=1
    g23: Circle CenterX=-6.77343 CenterY=-8 CenterZ=0 NormalX=0 NormalY=0 NormalZ=1 AngleXU=0 Radius=1
    g24: BSplineCurve PolesCount=3 KnotsCount=2 Degree=2 IsPeriodic=0
    g25: GeomPoint X=-6.48644 Y=-5.99526 Z=0
    g26: GeomPoint X=-6.77343 Y=-8 Z=0
    g27: Circle CenterX=-7.19003 CenterY=-10 CenterZ=0 NormalX=0 NormalY=0 NormalZ=1 AngleXU=0 Radius=1
    g28: Circle CenterX=-7.44407 CenterY=-11.0915 CenterZ=0 NormalX=0 NormalY=0 NormalZ=1 AngleXU=0 Radius=1
    g29: Circle CenterX=-7.79258 CenterY=-12 CenterZ=0 NormalX=0 NormalY=0 NormalZ=1 AngleXU=0 Radius=1
    g30: BSplineCurve PolesCount=3 KnotsCount=2 Degree=2 IsPeriodic=0
    g31: GeomPoint X=-7.19003 Y=-10 Z=0
    g32: GeomPoint X=-7.79258 Y=-12 Z=0
    g33: Circle CenterX=-8.70761 CenterY=-14 CenterZ=0 NormalX=0 NormalY=0 NormalZ=1 AngleXU=0 Radius=1
    g34: Circle CenterX=-9.33087 CenterY=-15.1837 CenterZ=0 NormalX=0 NormalY=0 NormalZ=1 AngleXU=0 Radius=1
    g35: Circle CenterX=-10.1571 CenterY=-16 CenterZ=0 NormalX=0 NormalY=0 NormalZ=1 AngleXU=0 Radius=1
    g36: BSplineCurve PolesCount=3 KnotsCount=2 Degree=2 IsPeriodic=0
    g37: GeomPoint X=-8.70761 Y=-14 Z=0
    g38: GeomPoint X=-10.1571 Y=-16 Z=0
    g39: Circle CenterX=-12.8401 CenterY=-17.6958 CenterZ=0 NormalX=0 NormalY=0 NormalZ=1 AngleXU=0 Radius=1
    g40: Circle CenterX=-13.3521 CenterY=-17.9027 CenterZ=0 NormalX=0 NormalY=0 NormalZ=1 AngleXU=0 Radius=1
    g41: Circle CenterX=-14 CenterY=-18 CenterZ=0 NormalX=0 NormalY=0 NormalZ=1 AngleXU=0 Radius=1
    g42: BSplineCurve PolesCount=3 KnotsCount=2 Degree=2 IsPeriodic=0
    g43: GeomPoint X=-12.8401 Y=-17.6958 Z=0
    g44: GeomPoint X=-14 Y=-18 Z=0
    g45: LineSegment StartX=-6.2 StartY=0 StartZ=0 EndX=-7.2 EndY=0 EndZ=0
    g46: LineSegment StartX=-7.2 StartY=0 StartZ=0 EndX=-7.2 EndY=-2 EndZ=0
    g47: LineSegment StartX=-7.2 StartY=-2 StartZ=0 EndX=-6.2215 EndY=-2 EndZ=0
    g48: LineSegment StartX=-6.32538 StartY=-4 StartZ=0 EndX=-7.65538 EndY=-4 EndZ=0
    g49: LineSegment StartX=-7.65538 StartY=-4 StartZ=0 EndX=-7.65538 EndY=-5.99526 EndZ=0
    g50: LineSegment StartX=-7.65538 StartY=-5.99526 StartZ=0 EndX=-6.48644 EndY=-5.99526 EndZ=0
    g51: LineSegment StartX=-6.77343 StartY=-8 StartZ=0 EndX=-8.43343 EndY=-8 EndZ=0
    g52: LineSegment StartX=-8.43343 StartY=-8 StartZ=0 EndX=-8.43343 EndY=-10 EndZ=0
    g53: LineSegment StartX=-8.43343 StartY=-10 StartZ=0 EndX=-7.19003 EndY=-10 EndZ=0
  constraints (112):
    c: Horizontal(g0)
    c: Distance(g0) = 2
    c: Block(g0)
    c: Vertical(g1)
    c: Coincident(g2,g0)
    c: Vertical(g2)
    c: Block(g2)
    c: Coincident(g6,g2)
    c: Weight(g3) = 1
    c: Equal(g3,g4)
    c: Equal(g3,g5)
    c: InternalAlignment(g3,g6)
    c: InternalAlignment(g4,g6)
    c: InternalAlignment(g5,g6)
    c: InternalAlignment(g7,g6)
    c: InternalAlignment(g8,g6)
    c: Block(g6)
    c: Coincident(g9,g1)
    c: Coincident(g9,g6)
    c: Horizontal(g9)
    c: Vertical(g10)
    c: Block(g10)
    c: Horizontal(g11)
    c: Block(g11)
    c: Coincident(g12,g10)
    c: Horizontal(g12)
    c: Block(g12)
    c: Coincident(g13,g11)
    c: Vertical(g13)
    c: Block(g13)
    c: Coincident(g14,g10)
    c: Horizontal(g14)
    c: Block(g14)
    c: Block(g9)
    c: Block(g1)
    c: Weight(g15) = 1
    c: Equal(g15,g16)
    c: Equal(g15,g17)
    c: InternalAlignment(g15,g18)
    c: InternalAlignment(g16,g18)
    c: InternalAlignment(g17,g18)
    c: InternalAlignment(g19,g18)
    c: InternalAlignment(g20,g18)
    c: Weight(g21) = 1
    c: Equal(g21,g22)
    c: Equal(g21,g23)
    c: InternalAlignment(g21,g24)
    c: InternalAlignment(g22,g24)
    c: InternalAlignment(g23,g24)
    c: InternalAlignment(g25,g24)
    c: InternalAlignment(g26,g24)
    c: Weight(g27) = 1
    c: Equal(g27,g28)
    c: Equal(g27,g29)
    c: Coincident(g30,g14)
    c: InternalAlignment(g27,g30)
    c: InternalAlignment(g28,g30)
    c: InternalAlignment(g29,g30)
    c: InternalAlignment(g31,g30)
    c: InternalAlignment(g32,g30)
    c: Coincident(g36,g12)
    c: Weight(g33) = 1
    c: Equal(g33,g34)
    c: Equal(g33,g35)
    c: Coincident(g36,g11)
    c: InternalAlignment(g33,g36)
    c: InternalAlignment(g34,g36)
    c: InternalAlignment(g35,g36)
    c: InternalAlignment(g37,g36)
    c: InternalAlignment(g38,g36)
    c: Coincident(g42,g13)
    c: Weight(g39) = 1
    c: Equal(g39,g40)
    c: Equal(g39,g41)
    c: Coincident(g42,g1)
    c: InternalAlignment(g39,g42)
    c: InternalAlignment(g40,g42)
    c: InternalAlignment(g41,g42)
    c: InternalAlignment(g43,g42)
    c: InternalAlignment(g44,g42)
    c: Block(g18)
    c: Block(g24)
    c: Block(g30)
    c: Block(g36)
    c: Block(g42)
    c: Horizontal(g45)
    c: Coincident(g45,g0)
    c: Vertical(g46)
    c: Coincident(g46,g45)
    c: Coincident(g47,g46)
    c: Coincident(g47,g18)
    c: Horizontal(g47)
    c: Block(g46)
    c: Coincident(g48,g18)
    c: Horizontal(g48)
    c: Distance(g48) = 1.33
    c: Vertical(g49)
    c: Coincident(g49,g48)
    c: Coincident(g50,g49)
    c: Coincident(g50,g24)
    c: Horizontal(g50)
    c: Tangent(g50,g22)
    c: Horizontal(g51)
    c: Coincident(g51,g24)
    c: Block(g51)
    c: Vertical(g52)
    c: Block(g52)
    c: Coincident(g52,g51)
    c: Coincident(g53,g52)
    c: Coincident(g53,g30)
    c: Horizontal(g53)
    c: Distance(g1) = 8.5
FEATURE [Part::Feature] Face024
  shape: bbox 9.8 x 26.5 x 2e-07 mm, 1 faces, 0 solids (baked)
FEATURE [Part::Revolution] Revolve024
  Angle = 360
  Axis = (0,1,0)
  Base = (0,0,0)
  FaceMakerClass = Part::FaceMakerBullseye
  Placement = pos=(0,0,0) rot=(0,0,1;1.5708rad)
  Solid = false
  Source = -> Face024
  Symmetric = false
FEATURE [Part::Feature] Face025
  shape: bbox 9.8 x 26.5 x 2e-07 mm, 1 faces, 0 solids (baked)
FEATURE [Part::Revolution] Revolve025
  Angle = 360
  Axis = (0,1,0)
  Base = (0,0,0)
  FaceMakerClass = Part::FaceMakerBullseye
  Placement = pos=(0,0,0) rot=(0,0,1;1.5708rad)
  Solid = false
  Source = -> Face025
  Symmetric = false
FEATURE [Part::MultiFuse] Fusion033
  Placement = pos=(-18,19,36) rot=(0,0,1;0rad)
  Shapes = -> [Revolve025,Revolve024]
FEATURE [Part::Cylinder] Cylinder014
  Angle = 360
  AttacherType = Attacher::AttachEngine3D
  Height = 20
  Placement = pos=(0,0,36.15) rot=(0,0,1;0rad)
  Radius = 14.3
FEATURE [Part::Cylinder] Cylinder015
  Angle = 360
  AttacherType = Attacher::AttachEngine3D
  Height = 10
  Placement = pos=(0,0,36.15) rot=(0,0,1;0rad)
  Radius = 4
FEATURE [Part::MultiFuse] Fusion034  label="removeToCreteHoleForPlugHousing004"
  Placement = pos=(-42,19,36) rot=(0,1,0;1.5708rad)
  Shapes = -> [Cylinder014,Cylinder015]
FEATURE [Part::Cut] Cut008  label="top004"
  Base = -> Cut004
  Placement = pos=(-1,0,0) rot=(0,0,1;0rad)
  Tool = -> Fusion034
FEATURE [Part::Box] Box005  label="Cube005"
  AttacherType = Attacher::AttachEngine3D
  Height = 28
  Length = 3
  Placement = pos=(110.7,19,22) rot=(0,0,1;0rad)
  Width = 15.7
FEATURE [Part::Cylinder] Cylinder016
  Angle = 360
  AttacherType = Attacher::AttachEngine3D
  Height = 10
  Placement = pos=(0,0,36.15) rot=(0,0,1;0rad)
  Radius = 4
FEATURE [Part::Cylinder] Cylinder017
  Angle = 360
  AttacherType = Attacher::AttachEngine3D
  Height = 20
  Placement = pos=(0,0,36.15) rot=(0,0,1;0rad)
  Radius = 10.3
FEATURE [Part::MultiFuse] Fusion035  label="removeToCreteHoleForPlugHousing005"
  Placement = pos=(70,19,36) rot=(0,1,0;1.5708rad)
  Shapes = -> [Cylinder017,Cylinder016]
FEATURE [Part::Cut] Cut009  label="plugHousingTab001"
  Base = -> Box005
  Placement = pos=(-107.4,-14,0) rot=(0,0,1;0rad)
  Tool = -> Fusion035
FEATURE [Part::Box] Box006  label="Cube006"
  AttacherType = Attacher::AttachEngine3D
  Height = 28
  Length = 3
  Placement = pos=(110.7,19,22) rot=(0,0,1;0rad)
  Width = 15.7
FEATURE [Part::Cylinder] Cylinder018
  Angle = 360
  AttacherType = Attacher::AttachEngine3D
  Height = 10
  Placement = pos=(0,0,36.15) rot=(0,0,1;0rad)
  Radius = 4
FEATURE [Part::Cylinder] Cylinder019
  Angle = 360
  AttacherType = Attacher::AttachEngine3D
  Height = 20
  Placement = pos=(0,0,36.15) rot=(0,0,1;0rad)
  Radius = 10.3
FEATURE [Part::MultiFuse] Fusion036  label="removeToCreteHoleForPlugHousing006"
  Placement = pos=(70,19,36) rot=(0,1,0;1.5708rad)
  Shapes = -> [Cylinder019,Cylinder018]
FEATURE [Part::Cut] Cut010  label="plugHousingTab002"
  Base = -> Box006
  Placement = pos=(-107.4,-14,0) rot=(0,0,1;0rad)
  Tool = -> Fusion036
FEATURE [Part::MultiFuse] Fusion037
  Placement = pos=(9.6,23,0) rot=(0,0,1;3.14159rad)
  Shapes = -> [Cut009,Cut010]
FEATURE [Part::Box] Box  label="Cube"
  AttacherType = Attacher::AttachEngine3D
  Height = 10
  Length = 3
  Placement = pos=(3.3,4,12) rot=(0,0,1;0rad)
  Width = 10
FEATURE [Part::Fillet] Fillet004
  Base = -> Fusion028
  Edges = 1 edges r=2: [Edge25]
FEATURE [Part::Fillet] Fillet005  label="plugHousing046"
  Base = -> Fillet004
  Edges = 1 edges r=2: [Edge8]
FEATURE [Part::Fillet] Fillet006
  Base = -> Box
  Edges = 1 edges r=2: [Edge11]
FEATURE [Part::Box] Box007  label="Cube007"
  AttacherType = Attacher::AttachEngine3D
  Height = 10
  Length = 3
  Placement = pos=(3.3,4,50) rot=(0,0,1;0rad)
  Width = 10
FEATURE [Part::Fillet] Fillet007
  Base = -> Box007
  Edges = 1 edges r=2: [Edge12]
FEATURE [Part::Box] Box008  label="Cube008"
  AttacherType = Attacher::AttachEngine3D
  Height = 28
  Length = 4
  Placement = pos=(5,0,22) rot=(0,0,1;0rad)
  Width = 10
FEATURE [Part::Fillet] Fillet008
  Base = -> Box008
  Edges = 1 edges r=1: [Edge7]
FEATURE [Part::Fillet] Fillet009
  Base = -> Fillet008
  Edges = 1 edges r=2: [Edge5]
FEATURE [Part::Fillet] Fillet010
  Base = -> Fillet009
  Edges = 1 edges r=2: [Edge2]
FEATURE [Sketcher::SketchObject] Sketch009  label="topSketch003"
  FullyConstrained = true
  sketch-geometry (4):
    g0: LineSegment StartX=16.8446 StartY=31.512 StartZ=0 EndX=16.3251 EndY=34.4666 EndZ=0
    g1: ArcOfCircle CenterX=19 CenterY=19.2524 CenterZ=0 NormalX=0 NormalY=0 NormalZ=1 AngleXU=0 Radius=15.4476 StartAngle=1.74483 EndAngle=2.72717
    g2: ArcOfCircle CenterX=19 CenterY=19.2524 CenterZ=0 NormalX=0 NormalY=0 NormalZ=1 AngleXU=0 Radius=12.4476 StartAngle=1.74483 EndAngle=2.73189
    g3: LineSegment StartX=4.86004 StartY=25.4725 StartZ=0 EndX=7.58253 EndY=24.2107 EndZ=0
  constraints (7):
    c: Block(g0)
    c: Coincident(g1,g0)
    c: Coincident(g2,g0)
    c: Coincident(g3,g1)
    c: Coincident(g3,g2)
    c: Block(g1)
    c: Block(g2)
FEATURE [Part::Extrusion] Extrude008
  Base = -> Sketch009
  Dir = (0,0,1)
  DirMode = 2
  FaceMakerClass = Part::FaceMakerBullseye
  LengthFwd = 10
  LengthRev = 0
  Placement = pos=(0,0,31) rot=(0,0,1;0rad)
  Solid = true
  Symmetric = false
FEATURE [Part::Cylinder] Cylinder020
  Angle = 360
  AttacherType = Attacher::AttachEngine3D
  Height = 20
  Placement = pos=(0,0,36.15) rot=(0,0,1;0rad)
  Radius = 8.2
FEATURE [Part::Cylinder] Cylinder021
  Angle = 360
  AttacherType = Attacher::AttachEngine3D
  Height = 10
  Placement = pos=(0,0,36.15) rot=(0,0,1;0rad)
  Radius = 4
FEATURE [Part::MultiFuse] Fusion038  label="removeToCreteHoleForPlugHousing007"
  Placement = pos=(-42,19,36) rot=(0,1,0;1.5708rad)
  Shapes = -> [Cylinder020,Cylinder021]
FEATURE [Part::Cut] Cut011
  Base = -> Extrude008
  Tool = -> Fusion038
FEATURE [Part::Fillet] Fillet011
  Base = -> Cut011
  Edges = 1 edges r=2: [Edge1]
FEATURE [Part::Fillet] Fillet012
  Base = -> Fillet011
  Edges = 1 edges r=2.5: [Edge1]
FEATURE [Part::Fillet] Fillet013
  Base = -> Fillet012
  Edges = 1 edges r=2.5: [Edge2]
FEATURE [Part::Box] Box010  label="Cube010"
  AttacherType = Attacher::AttachEngine3D
  Height = 16
  Length = 8
  Placement = pos=(12.7,31.52,28) rot=(0,0,1;0rad)
  Width = 4
FEATURE [Sketcher::SketchObject] Sketch010  label="topSketch004"
  FullyConstrained = true
  sketch-geometry (4):
    g0: LineSegment StartX=16.8446 StartY=31.512 StartZ=0 EndX=16.3251 EndY=34.4666 EndZ=0
    g1: ArcOfCircle CenterX=19 CenterY=19.2524 CenterZ=0 NormalX=0 NormalY=0 NormalZ=1 AngleXU=0 Radius=15.4476 StartAngle=1.74483 EndAngle=2.72717
    g2: ArcOfCircle CenterX=19 CenterY=19.2524 CenterZ=0 NormalX=0 NormalY=0 NormalZ=1 AngleXU=0 Radius=12.4476 StartAngle=1.74483 EndAngle=2.73189
    g3: LineSegment StartX=4.86004 StartY=25.4725 StartZ=0 EndX=7.58253 EndY=24.2107 EndZ=0
  constraints (7):
    c: Block(g0)
    c: Coincident(g1,g0)
    c: Coincident(g2,g0)
    c: Coincident(g3,g1)
    c: Coincident(g3,g2)
    c: Block(g1)
    c: Block(g2)
FEATURE [Part::Cylinder] Cylinder022
  Angle = 360
  AttacherType = Attacher::AttachEngine3D
  Height = 10
  Placement = pos=(0,0,36.15) rot=(0,0,1;0rad)
  Radius = 4
FEATURE [Sketcher::SketchObject] Sketch011  label="topSketch005"
  FullyConstrained = true
  sketch-geometry (4):
    g0: LineSegment StartX=16.8446 StartY=31.512 StartZ=0 EndX=16.3251 EndY=34.4666 EndZ=0
    g1: ArcOfCircle CenterX=19 CenterY=19.2524 CenterZ=0 NormalX=0 NormalY=0 NormalZ=1 AngleXU=0 Radius=15.4476 StartAngle=1.74483 EndAngle=2.72717
    g2: ArcOfCircle CenterX=19 CenterY=19.2524 CenterZ=0 NormalX=0 NormalY=0 NormalZ=1 AngleXU=0 Radius=12.4476 StartAngle=1.74483 EndAngle=2.73189
    g3: LineSegment StartX=4.86004 StartY=25.4725 StartZ=0 EndX=7.58253 EndY=24.2107 EndZ=0
  constraints (7):
    c: Block(g0)
    c: Coincident(g1,g0)
    c: Coincident(g2,g0)
    c: Coincident(g3,g1)
    c: Coincident(g3,g2)
    c: Block(g1)
    c: Block(g2)
FEATURE [Part::Extrusion] Extrude010
  Base = -> Sketch011
  Dir = (0,0,1)
  DirMode = 2
  FaceMakerClass = Part::FaceMakerBullseye
  LengthFwd = 10.6
  LengthRev = 0
  Placement = pos=(0,0,31) rot=(0,0,1;0rad)
  Solid = true
  Symmetric = false
FEATURE [Part::Cylinder] Cylinder023
  Angle = 360
  AttacherType = Attacher::AttachEngine3D
  Height = 20
  Placement = pos=(0,0,36.15) rot=(0,0,1;0rad)
  Radius = 8.2
FEATURE [Part::MultiFuse] Fusion039  label="removeToCreteHoleForPlugHousing008"
  Placement = pos=(-42,19,36) rot=(0,1,0;1.5708rad)
  Shapes = -> [Cylinder023,Cylinder022]
FEATURE [Part::Cut] Cut012
  Base = -> Extrude010
  Placement = pos=(0,0,-0.3) rot=(0,0,1;0rad)
  Tool = -> Fusion039
FEATURE [Part::Cut] Cut013
  Base = -> Box010
  Tool = -> Cut012
FEATURE [Part::Fillet] Fillet014
  Base = -> Cut013
  Edges = 1 edges r=0.7: [Edge13]
FEATURE [Part::Fillet] Fillet015
  Base = -> Fillet014
  Edges = 1 edges r=0.7: [Edge13]
FEATURE [Part::Fillet] Fillet016
  Base = -> Fillet015
  Edges = 1 edges r=0.7: [Edge16]
FEATURE [Part::Fillet] Fillet017
  Base = -> Fillet016
  Edges = 1 edges r=0.7: [Edge11]
FEATURE [Part::Fillet] Fillet018
  Base = -> Fillet017
  Edges = 1 edges r=0.7: [Edge10]
FEATURE [Part::Fillet] Fillet019
  Base = -> Fillet018
  Edges = 1 edges r=1.2: [Edge5]
FEATURE [Part::Fillet] Fillet020
  Base = -> Fillet019
  Edges = 1 edges r=1.2: [Edge12]
FEATURE [Part::Fillet] Fillet021
  Base = -> Fillet020
  Edges = 1 edges r=2: [Edge1]
  Placement = pos=(0.3,0,0) rot=(0,0,1;0rad)
FEATURE [Part::MultiFuse] Fusion040  label="top005"
  Shapes = -> [Cut008,Fillet021]
FEATURE [Part::MultiFuse] Fusion041  label="wireHolder"
  Shapes = -> [Fusion033,Fillet013]
FEATURE [Part::MultiFuse] Fusion042
  Shapes = -> [Fillet007,Fusion041]
FEATURE [Part::MultiFuse] Fusion043  label="wireHolder001"
  Shapes = -> [Fusion042,Fillet010]
FEATURE [Part::MultiFuse] Fusion044  label="wireHolder002"
  Shapes = -> [Fillet006,Fusion037,Fusion043]
FEATURE [Part::Feature] Face026
  shape: bbox 11 x 6 x 2e-07 mm, 1 faces, 0 solids (baked)
FEATURE [Part::Revolution] Revolve026
  Angle = 360
  Axis = (0,1,0)
  Base = (0,0,0)
  FaceMakerClass = Part::FaceMakerBullseye
  Placement = pos=(30.3,-1,19.7) rot=(0,0,1;0rad)
  Solid = false
  Source = -> Face026
  Symmetric = false
FEATURE [Sketcher::SketchObject] Sketch013  label="topSketch006"
  FullyConstrained = true
  sketch-geometry (13):
    g0: LineSegment StartX=117 StartY=19 StartZ=0 EndX=117 EndY=38 EndZ=0
    g1: ArcOfCircle CenterX=98 CenterY=19 CenterZ=0 NormalX=0 NormalY=0 NormalZ=1 AngleXU=0 Radius=19 StartAngle=5.7297 EndAngle=6.28319
    g2: LineSegment StartX=0 StartY=3 StartZ=0 EndX=0 EndY=19 EndZ=0
    g3: LineSegment StartX=19 StartY=38 StartZ=0 EndX=117 EndY=38 EndZ=0
    g4: ArcOfCircle CenterX=19 CenterY=19 CenterZ=0 NormalX=0 NormalY=0 NormalZ=1 AngleXU=0 Radius=19 StartAngle=1.5708 EndAngle=3.14159
    g5: ArcOfCircle CenterX=19 CenterY=19 CenterZ=0 NormalX=0 NormalY=0 NormalZ=1 AngleXU=0 Radius=16 StartAngle=1.5708 EndAngle=3.14159
    g6: ArcOfCircle CenterX=98 CenterY=19 CenterZ=0 NormalX=0 NormalY=0 NormalZ=1 AngleXU=0 Radius=16 StartAngle=5.60905 EndAngle=6.28319
    g7: LineSegment StartX=114 StartY=19 StartZ=0 EndX=114 EndY=35 EndZ=0
    g8: LineSegment StartX=110.5 StartY=9.01251 StartZ=0 EndX=114.163 EndY=9.01251 EndZ=0
    g9: LineSegment StartX=114 StartY=35 StartZ=0 EndX=19 EndY=35 EndZ=0
    g10: LineSegment StartX=0 StartY=3 StartZ=0 EndX=0 EndY=0 EndZ=0
    g11: LineSegment StartX=3 StartY=0 StartZ=0 EndX=0 EndY=0 EndZ=0
    g12: LineSegment StartX=3 StartY=19 StartZ=0 EndX=3 EndY=0 EndZ=0
  constraints (33):
    c: Vertical(g0)
    c: Distance(g0) = 19
    c: Block(g0)
    c: Coincident(g1,g0)
    c: Block(g1)
    c: Vertical(g2)
    c: Block(g2)
    c: Coincident(g3,g0)
    c: Horizontal(g3)
    c: Distance(g3) = 98
    c: Coincident(g4,g3)
    c: Coincident(g4,g2)
    c: Block(g4)
    c: Coincident(g5,g4)
    c: Coincident(g6,g1)
    c: Block(g6)
    c: Block(g5)
    c: Coincident(g7,g6)
    c: Vertical(g7)
    c: Coincident(g8,g6)
    c: Coincident(g8,g1)
    c: Coincident(g9,g7)
    c: Coincident(g9,g5)
    c: Horizontal(g9)
    c: Tangent(g9,g5)
    c: Coincident(g10,g2)
    c: Distance(g10) = 3
    c: Vertical(g10)
    c: Coincident(g11,g10)
    c: Horizontal(g11)
    c: Coincident(g12,g5)
    c: Coincident(g12,g11)
    c: Vertical(g12)
FEATURE [Part::Extrusion] Extrude011  label="top006"
  Base = -> Sketch013
  Dir = (0,0,1)
  DirMode = 2
  FaceMakerClass = Part::FaceMakerBullseye
  LengthFwd = 72
  LengthRev = 0
  Solid = true
  Symmetric = false
FEATURE [Sketcher::SketchObject] Sketch014
  FullyConstrained = true
  MapMode = 3
  Placement = pos=(0,0,0) rot=(1,0,0;1.5708rad)
  Support = -> [Extrude011]
  sketch-geometry (8):
    g0: Circle CenterX=80.351 CenterY=-67.6202 CenterZ=0 NormalX=0 NormalY=0 NormalZ=1 AngleXU=0 Radius=2
    g1: Circle CenterX=80.351 CenterY=-67.6202 CenterZ=0 NormalX=0 NormalY=0 NormalZ=1 AngleXU=0 Radius=3
    g2: Circle CenterX=80.351 CenterY=-4.92017 CenterZ=0 NormalX=0 NormalY=0 NormalZ=1 AngleXU=0 Radius=2
    g3: Circle CenterX=80.351 CenterY=-4.92017 CenterZ=0 NormalX=0 NormalY=0 NormalZ=1 AngleXU=0 Radius=3
    g4: Circle CenterX=23.851 CenterY=-4.92017 CenterZ=0 NormalX=0 NormalY=0 NormalZ=1 AngleXU=0 Radius=2
    g5: Circle CenterX=23.851 CenterY=-4.92017 CenterZ=0 NormalX=0 NormalY=0 NormalZ=1 AngleXU=0 Radius=3
    g6: Circle CenterX=23.851 CenterY=-67.6202 CenterZ=0 NormalX=0 NormalY=0 NormalZ=1 AngleXU=0 Radius=2
    g7: Circle CenterX=23.851 CenterY=-67.6202 CenterZ=0 NormalX=0 NormalY=0 NormalZ=1 AngleXU=0 Radius=3
  constraints (8):
    c: Block(g3)
    c: Block(g2)
    c: Block(g1)
    c: Block(g0)
    c: Block(g6)
    c: Block(g7)
    c: Block(g4)
    c: Block(g5)
FEATURE [Part::Feature] Face027
  shape: bbox 11 x 6 x 2e-07 mm, 1 faces, 0 solids (baked)
FEATURE [Part::Revolution] Revolve027
  Angle = 360
  Axis = (0,1,0)
  Base = (0,0,0)
  FaceMakerClass = Part::FaceMakerBullseye
  Placement = pos=(30.3,-1,51.7) rot=(0,0,1;0rad)
  Solid = false
  Source = -> Face027
  Symmetric = false
FEATURE [Part::Feature] Face028
  shape: bbox 11 x 6 x 2e-07 mm, 1 faces, 0 solids (baked)
FEATURE [Part::Revolution] Revolve028
  Angle = 360
  Axis = (0,1,0)
  Base = (0,0,0)
  FaceMakerClass = Part::FaceMakerBullseye
  Placement = pos=(62.3,-1,19.7) rot=(0,0,1;0rad)
  Solid = false
  Source = -> Face028
  Symmetric = false
FEATURE [Part::Feature] Face029
  shape: bbox 11 x 6 x 2e-07 mm, 1 faces, 0 solids (baked)
FEATURE [Part::Revolution] Revolve029
  Angle = 360
  Axis = (0,1,0)
  Base = (0,0,0)
  FaceMakerClass = Part::FaceMakerBullseye
  Placement = pos=(62.3,-1,51.7) rot=(0,0,1;0rad)
  Solid = false
  Source = -> Face029
  Symmetric = false
FEATURE [Part::Feature] Wire
  shape: bbox 11 x 5.2 x 2e-07 mm, 0 faces, 0 solids (baked)
FEATURE [Part::Revolution] Revolve030
  Angle = 360
  Axis = (0,1,0)
  Base = (0,0,0)
  FaceMakerClass = Part::FaceMakerBullseye
  Placement = pos=(30.3,38,19.7) rot=(0,0,1;0rad)
  Solid = true
  Source = -> Wire
  Symmetric = false
FEATURE [Part::Feature] Wire001
  shape: bbox 11 x 5.2 x 2e-07 mm, 0 faces, 0 solids (baked)
FEATURE [Part::Revolution] Revolve031
  Angle = 360
  Axis = (0,1,0)
  Base = (0,0,0)
  FaceMakerClass = Part::FaceMakerBullseye
  Placement = pos=(30.3,38,51.7) rot=(0,0,1;0rad)
  Solid = true
  Source = -> Wire001
  Symmetric = false
FEATURE [Part::Feature] Wire002
  shape: bbox 11 x 5.2 x 2e-07 mm, 0 faces, 0 solids (baked)
FEATURE [Part::Revolution] Revolve032
  Angle = 360
  Axis = (0,1,0)
  Base = (0,0,0)
  FaceMakerClass = Part::FaceMakerBullseye
  Placement = pos=(62.3,38,51.7) rot=(0,0,1;0rad)
  Solid = true
  Source = -> Wire002
  Symmetric = false
FEATURE [Part::Feature] Wire003
  shape: bbox 11 x 5.2 x 2e-07 mm, 0 faces, 0 solids (baked)
FEATURE [Part::Revolution] Revolve033
  Angle = 360
  Axis = (0,1,0)
  Base = (0,0,0)
  FaceMakerClass = Part::FaceMakerBullseye
  Placement = pos=(62.3,38,19.7) rot=(0,0,1;0rad)
  Solid = true
  Source = -> Wire003
  Symmetric = false
FEATURE [Part::MultiFuse] Fusion045  label="altRandScrewHousing"
  Shapes = -> [Revolve029,Revolve027,Revolve028,Revolve026]
FEATURE [Part::MultiFuse] Fusion046  label="fanScrewHousing"
  Shapes = -> [Revolve033,Revolve032,Revolve031,Revolve030]
FEATURE [Sketcher::SketchObject] Sketch015
  FullyConstrained = true
  sketch-geometry (17):
    g0: Circle CenterX=-3.5 CenterY=23.5 CenterZ=0 NormalX=0 NormalY=0 NormalZ=1 AngleXU=0 Radius=1
    g1: Circle CenterX=-1 CenterY=15.25 CenterZ=0 NormalX=0 NormalY=0 NormalZ=1 AngleXU=0 Radius=1
    g2: Circle CenterX=-3.5 CenterY=7 CenterZ=0 NormalX=0 NormalY=0 NormalZ=1 AngleXU=0 Radius=1
    g3: BSplineCurve PolesCount=3 KnotsCount=2 Degree=2 IsPeriodic=0
    g4: GeomPoint X=-3.5 Y=23.5 Z=0
    g5: GeomPoint X=-3.5 Y=7 Z=0
    g6: Circle CenterX=-4.8 CenterY=30.5 CenterZ=0 NormalX=0 NormalY=0 NormalZ=1 AngleXU=0 Radius=1
    g7: Circle CenterX=-3.5 CenterY=30.5 CenterZ=0 NormalX=0 NormalY=0 NormalZ=1 AngleXU=0 Radius=1
    g8: Circle CenterX=-3.5 CenterY=29.2 CenterZ=0 NormalX=0 NormalY=0 NormalZ=1 AngleXU=0 Radius=1
    g9: BSplineCurve PolesCount=3 KnotsCount=2 Degree=2 IsPeriodic=0
    g10: GeomPoint X=-4.8 Y=30.5 Z=0
    g11: GeomPoint X=-3.5 Y=29.2 Z=0
    g12: LineSegment StartX=-3.5 StartY=29.2 StartZ=0 EndX=-3.5 EndY=23.5 EndZ=0
    g13: LineSegment StartX=-4.8 StartY=30.5 StartZ=0 EndX=0 EndY=30.5 EndZ=0
    g14: LineSegment StartX=-3.5 StartY=0.3 StartZ=0 EndX=0 EndY=0.3 EndZ=0
    g15: LineSegment StartX=-3.5 StartY=0.3 StartZ=0 EndX=-3.5 EndY=7 EndZ=0
    g16: LineSegment StartX=0 StartY=0.3 StartZ=0 EndX=0 EndY=30.5 EndZ=0
  constraints (33):
    c: Weight(g0) = 1
    c: Equal(g0,g1)
    c: Equal(g0,g2)
    c: InternalAlignment(g0,g3)
    c: InternalAlignment(g1,g3)
    c: InternalAlignment(g2,g3)
    c: InternalAlignment(g4,g3)
    c: InternalAlignment(g5,g3)
    c: Block(g3)
    c: Weight(g6) = 1
    c: Equal(g6,g7)
    c: Equal(g6,g8)
    c: InternalAlignment(g6,g9)
    c: InternalAlignment(g7,g9)
    c: InternalAlignment(g8,g9)
    c: InternalAlignment(g10,g9)
    c: InternalAlignment(g11,g9)
    c: Block(g9)
    c: Coincident(g12,g9)
    c: Coincident(g12,g3)
    c: Vertical(g12)
    c: Coincident(g13,g9)
    c: Horizontal(g13)
    c: Distance(g13) = 4.8
    c: Horizontal(g14)
    c: Block(g14)
    c: Coincident(g15,g14)
    c: Coincident(g15,g3)
    c: Vertical(g15)
    c: Coincident(g16,g14)
    c: Coincident(g16,g13)
    c: Vertical(g16)
    c: Tangent(g16,g1)
FEATURE [Sketcher::SketchObject] Sketch016
  FullyConstrained = true
  sketch-geometry (15):
    g0: LineSegment StartX=0 StartY=0 StartZ=0 EndX=-3.5 EndY=0 EndZ=0
    g1: LineSegment StartX=-3.5 StartY=0 StartZ=0 EndX=-3.5 EndY=7 EndZ=0
    g2: Circle CenterX=-3.5 CenterY=23.5 CenterZ=0 NormalX=0 NormalY=0 NormalZ=1 AngleXU=0 Radius=1
    g3: Circle CenterX=-1 CenterY=15.25 CenterZ=0 NormalX=0 NormalY=0 NormalZ=1 AngleXU=0 Radius=1
    g4: Circle CenterX=-3.5 CenterY=7 CenterZ=0 NormalX=0 NormalY=0 NormalZ=1 AngleXU=0 Radius=1
    g5: BSplineCurve PolesCount=3 KnotsCount=2 Degree=2 IsPeriodic=0
    g6: GeomPoint X=-3.5 Y=23.5 Z=0
    g7: GeomPoint X=-3.5 Y=7 Z=0
    g8: LineSegment StartX=-3.5 StartY=28.2 StartZ=0 EndX=-3.5 EndY=23.5 EndZ=0
    g9: LineSegment StartX=0 StartY=0 StartZ=0 EndX=0 EndY=29.5 EndZ=0
    g10: LineSegment StartX=0 StartY=29.5 StartZ=0 EndX=0 EndY=30 EndZ=0
    g11: LineSegment StartX=-3.5 StartY=28.2 StartZ=0 EndX=-3.5 EndY=30 EndZ=0
    g12: LineSegment StartX=0 StartY=30 StartZ=0 EndX=0 EndY=30.5 EndZ=0
    g13: LineSegment StartX=0 StartY=30.5 StartZ=0 EndX=-3.5 EndY=30.5 EndZ=0
    g14: LineSegment StartX=-3.5 StartY=30.5 StartZ=0 EndX=-3.5 EndY=30 EndZ=0
  constraints (39):
    c: Coincident(g0,g-1)
    c: Horizontal(g0)
    c: Distance(g0) = 3.5
    c: Coincident(g1,g0)
    c: Vertical(g1)
    c: Distance(g1) = 7
    c: Weight(g2) = 1
    c: Equal(g2,g3)
    c: Equal(g2,g4)
    c: Coincident(g5,g1)
    c: InternalAlignment(g2,g5)
    c: InternalAlignment(g3,g5)
    c: InternalAlignment(g4,g5)
    c: InternalAlignment(g6,g5)
    c: InternalAlignment(g7,g5)
    c: Block(g5)
    c: Coincident(g8,g5)
    c: Vertical(g8)
    c: Coincident(g9,g0)
    c: Vertical(g9)
    c: Tangent(g9,g3)
    c: Vertical(g10)
    c: Distance(g10) = 0.5
    c: Coincident(g11,g8)
    c: Vertical(g11)
    c: Block(g9)
    c: Block(g8)
    c: Block(g10)
    c: Vertical(g12)
    c: Equal(g10,g12) = 0.5
    c: Block(g12)
    c: Coincident(g12,g10)
    c: Horizontal(g13)
    c: Coincident(g13,g12)
    c: Coincident(g14,g13)
    c: Coincident(g14,g11)
    c: Vertical(g14)
    c: Block(g14)
    c: Distance(g9) = 29.5
FEATURE [Sketcher::SketchObject] Sketch017
  FullyConstrained = true
  sketch-geometry (11):
    g0: LineSegment StartX=-3.5 StartY=1e-16 StartZ=0 EndX=-1.6 EndY=1e-16 EndZ=0
    g1: LineSegment StartX=-1.6 StartY=1e-16 StartZ=0 EndX=-1.6 EndY=1.5 EndZ=0
    g2: LineSegment StartX=-3.5 StartY=1.5 StartZ=0 EndX=-1.6 EndY=1.5 EndZ=0
    g3: LineSegment StartX=-3.5 StartY=1e-16 StartZ=0 EndX=-4.8 EndY=1e-16 EndZ=0
    g4: Circle CenterX=-3.5 CenterY=1.3 CenterZ=0 NormalX=0 NormalY=0 NormalZ=1 AngleXU=0 Radius=1
    g5: Circle CenterX=-3.5 CenterY=1e-16 CenterZ=0 NormalX=0 NormalY=0 NormalZ=1 AngleXU=0 Radius=1
    g6: Circle CenterX=-4.8 CenterY=1e-16 CenterZ=0 NormalX=0 NormalY=0 NormalZ=1 AngleXU=0 Radius=1
    g7: BSplineCurve PolesCount=3 KnotsCount=2 Degree=2 IsPeriodic=0
    g8: GeomPoint X=-3.5 Y=1.3 Z=0
    g9: GeomPoint X=-4.8 Y=1e-16 Z=0
    g10: LineSegment StartX=-3.5 StartY=1.3 StartZ=0 EndX=-3.5 EndY=1.5 EndZ=0
  constraints (24):
    c: Horizontal(g0)
    c: Distance(g0) = 1.9
    c: Block(g0)
    c: Coincident(g1,g0)
    c: Vertical(g1)
    c: Coincident(g2,g1)
    c: Horizontal(g2)
    c: Coincident(g3,g0)
    c: Horizontal(g3)
    c: Distance(g3) = 1.3
    c: Weight(g4) = 1
    c: Equal(g4,g5)
    c: Coincident(g5,g0)
    c: Equal(g4,g6)
    c: Coincident(g7,g3)
    c: InternalAlignment(g4,g7)
    c: InternalAlignment(g5,g7)
    c: InternalAlignment(g6,g7)
    c: InternalAlignment(g8,g7)
    c: InternalAlignment(g9,g7)
    c: Coincident(g10,g7)
    c: Coincident(g10,g2)
    c: Vertical(g10)
    c: Block(g10)
FEATURE [Part::Feature] Face035
  shape: bbox 3.2 x 1.5 x 2e-07 mm, 1 faces, 0 solids (baked)
FEATURE [Part::Revolution] Revolve039  label="backCaseScrewRetainer"
  Angle = 360
  Axis = (0,1,0)
  Base = (0,0,0)
  FaceMakerClass = Part::FaceMakerBullseye
  Placement = pos=(12.5,3,62) rot=(0,0,1;0rad)
  Solid = false
  Source = -> Face035
  Symmetric = false
FEATURE [Part::Feature] Face036
  shape: bbox 3.2 x 1.5 x 2e-07 mm, 1 faces, 0 solids (baked)
FEATURE [Part::Revolution] Revolve040  label="backCaseScrewRetainer001"
  Angle = 360
  Axis = (0,1,0)
  Base = (0,0,0)
  FaceMakerClass = Part::FaceMakerBullseye
  Placement = pos=(12.5,3,10) rot=(0,0,1;0rad)
  Solid = false
  Source = -> Face036
  Symmetric = false
FEATURE [Part::Feature] Face039
  shape: bbox 4.8 x 30.2 x 2e-07 mm, 1 faces, 0 solids (baked)
FEATURE [Part::Revolution] Revolve043  label="frontCaseScrewPost002"
  Angle = 360
  Axis = (0,1,0)
  Base = (0,0,0)
  FaceMakerClass = Part::FaceMakerBullseye
  Placement = pos=(89.5,4.5,3.5) rot=(0,0,1;0rad)
  Solid = false
  Source = -> Face039
  Symmetric = false
FEATURE [Part::Feature] Face040
  shape: bbox 4.8 x 30.2 x 2e-07 mm, 1 faces, 0 solids (baked)
FEATURE [Part::Revolution] Revolve044  label="moreFrontCaseScrewPost"
  Angle = 360
  Axis = (0,1,0)
  Base = (0,0,0)
  FaceMakerClass = Part::FaceMakerBullseye
  Placement = pos=(102.5,4.5,68.5) rot=(0,0,1;0rad)
  Solid = false
  Source = -> Face040
  Symmetric = false
FEATURE [Part::Feature] Face041
  shape: bbox 4.8 x 30.2 x 2e-07 mm, 1 faces, 0 solids (baked)
FEATURE [Part::Revolution] Revolve045  label="moreFrontCaseScrewPost004"
  Angle = 360
  Axis = (0,1,0)
  Base = (0,0,0)
  FaceMakerClass = Part::FaceMakerBullseye
  Placement = pos=(102.5,4.5,3.5) rot=(0,0,1;0rad)
  Solid = false
  Source = -> Face041
  Symmetric = false
FEATURE [Part::Feature] Face042
  shape: bbox 4.8 x 30.2 x 2e-07 mm, 1 faces, 0 solids (baked)
FEATURE [Part::Revolution] Revolve046  label="frontCaseScrewPost003"
  Angle = 360
  Axis = (0,1,0)
  Base = (0,0,0)
  FaceMakerClass = Part::FaceMakerBullseye
  Placement = pos=(89.5,4.5,68.5) rot=(0,0,1;0rad)
  Solid = false
  Source = -> Face042
  Symmetric = false
FEATURE [Part::Feature] Face043
  shape: bbox 3.2 x 1.5 x 2e-07 mm, 1 faces, 0 solids (baked)
FEATURE [Part::Revolution] Revolve047  label="frontCaseScrewRetainer002"
  Angle = 360
  Axis = (0,1,0)
  Base = (0,0,0)
  FaceMakerClass = Part::FaceMakerBullseye
  Placement = pos=(89.5,3,68.5) rot=(0,0,1;0rad)
  Solid = false
  Source = -> Face043
  Symmetric = false
FEATURE [Part::Feature] Face044
  shape: bbox 3.2 x 1.5 x 2e-07 mm, 1 faces, 0 solids (baked)
FEATURE [Part::Revolution] Revolve048  label="frontCaseScrewRetainer003"
  Angle = 360
  Axis = (0,1,0)
  Base = (0,0,0)
  FaceMakerClass = Part::FaceMakerBullseye
  Placement = pos=(89.5,3,3.5) rot=(0,0,1;0rad)
  Solid = false
  Source = -> Face044
  Symmetric = false
FEATURE [App::MeasureDistance] Distance002  label="Distance: 1.67 mm"
  Distance = 1.66921
  P1 = (99.2361,4.7524,71.7)
  P2 = (99.2347,6.42161,71.7)
FEATURE [Part::Feature] Face047
  shape: bbox 3.5 x 30.5 x 2e-07 mm, 1 faces, 0 solids (baked)
FEATURE [Part::Revolution] Revolve051  label="backCaseScrewPost"
  Angle = 360
  Axis = (0,1,0)
  Base = (0,0,0)
  FaceMakerClass = Part::FaceMakerBullseye
  Placement = pos=(12.5,4.5,10) rot=(0,0,1;0rad)
  Solid = false
  Source = -> Face047
  Symmetric = false
FEATURE [Part::Feature] Face048
  shape: bbox 3.5 x 30.5 x 2e-07 mm, 1 faces, 0 solids (baked)
FEATURE [Part::Revolution] Revolve052  label="backCaseScrewPost003"
  Angle = 360
  Axis = (0,1,0)
  Base = (0,0,0)
  FaceMakerClass = Part::FaceMakerBullseye
  Placement = pos=(12.5,4.5,62) rot=(0,0,1;0rad)
  Solid = false
  Source = -> Face048
  Symmetric = false
FEATURE [Sketcher::SketchObject] Sketch018
  FullyConstrained = true
  sketch-geometry (7):
    g0: LineSegment StartX=0 StartY=0 StartZ=0 EndX=0 EndY=6 EndZ=0
    g1: Circle CenterX=0 CenterY=0 CenterZ=0 NormalX=0 NormalY=0 NormalZ=1 AngleXU=0 Radius=1
    g2: Circle CenterX=8 CenterY=6 CenterZ=0 NormalX=0 NormalY=0 NormalZ=1 AngleXU=0 Radius=1
    g3: BSplineCurve PolesCount=3 KnotsCount=2 Degree=2 IsPeriodic=0
    g4: GeomPoint X=0 Y=0 Z=0
    g5: GeomPoint X=8 Y=6 Z=0
    g6: LineSegment StartX=0 StartY=6 StartZ=0 EndX=8 EndY=6 EndZ=0
  constraints (14):
    c: Coincident(g0,g-1)
    c: Distance(g0) = 6
    c: Vertical(g0)
    c: Coincident(g3,g0)
    c: Weight(g1) = 1
    c: Equal(g1,g2)
    c: InternalAlignment(g1,g3)
    c: InternalAlignment(g2,g3)
    c: InternalAlignment(g4,g3)
    c: InternalAlignment(g5,g3)
    c: Block(g3)
    c: Coincident(g6,g0)
    c: Coincident(g6,g3)
    c: Horizontal(g6)
FEATURE [Part::Extrusion] Extrude012  label="caseScrewPillarBracket"
  Base = -> Sketch018
  Dir = (0,0,1)
  DirMode = 2
  FaceMakerClass = Part::FaceMakerBullseye
  LengthFwd = 2.4
  LengthRev = 0
  Placement = pos=(15.76,29,8.8) rot=(0,1,0;0rad)
  Solid = true
  Symmetric = false
FEATURE [Sketcher::SketchObject] Sketch019
  FullyConstrained = true
  sketch-geometry (7):
    g0: LineSegment StartX=0 StartY=0 StartZ=0 EndX=0 EndY=6 EndZ=0
    g1: Circle CenterX=0 CenterY=0 CenterZ=0 NormalX=0 NormalY=0 NormalZ=1 AngleXU=0 Radius=1
    g2: Circle CenterX=8 CenterY=6 CenterZ=0 NormalX=0 NormalY=0 NormalZ=1 AngleXU=0 Radius=1
    g3: BSplineCurve PolesCount=3 KnotsCount=2 Degree=2 IsPeriodic=0
    g4: GeomPoint X=0 Y=0 Z=0
    g5: GeomPoint X=8 Y=6 Z=0
    g6: LineSegment StartX=0 StartY=6 StartZ=0 EndX=8 EndY=6 EndZ=0
  constraints (14):
    c: Coincident(g0,g-1)
    c: Distance(g0) = 6
    c: Vertical(g0)
    c: Coincident(g3,g0)
    c: Weight(g1) = 1
    c: Equal(g1,g2)
    c: InternalAlignment(g1,g3)
    c: InternalAlignment(g2,g3)
    c: InternalAlignment(g4,g3)
    c: InternalAlignment(g5,g3)
    c: Block(g3)
    c: Coincident(g6,g0)
    c: Coincident(g6,g3)
    c: Horizontal(g6)
FEATURE [Part::Extrusion] Extrude013  label="caseScrewPillarBracket001"
  Base = -> Sketch019
  Dir = (0,0,1)
  DirMode = 2
  FaceMakerClass = Part::FaceMakerBullseye
  LengthFwd = 2.4
  LengthRev = 0
  Placement = pos=(15.76,29,60.8) rot=(0,0,1;0rad)
  Solid = true
  Symmetric = false
FEATURE [Sketcher::SketchObject] Sketch020
  FullyConstrained = true
  sketch-geometry (7):
    g0: LineSegment StartX=0 StartY=0 StartZ=0 EndX=0 EndY=6 EndZ=0
    g1: Circle CenterX=0 CenterY=0 CenterZ=0 NormalX=0 NormalY=0 NormalZ=1 AngleXU=0 Radius=1
    g2: Circle CenterX=8 CenterY=6 CenterZ=0 NormalX=0 NormalY=0 NormalZ=1 AngleXU=0 Radius=1
    g3: BSplineCurve PolesCount=3 KnotsCount=2 Degree=2 IsPeriodic=0
    g4: GeomPoint X=0 Y=0 Z=0
    g5: GeomPoint X=8 Y=6 Z=0
    g6: LineSegment StartX=0 StartY=6 StartZ=0 EndX=8 EndY=6 EndZ=0
  constraints (14):
    c: Coincident(g0,g-1)
    c: Distance(g0) = 6
    c: Vertical(g0)
    c: Coincident(g3,g0)
    c: Weight(g1) = 1
    c: Equal(g1,g2)
    c: InternalAlignment(g1,g3)
    c: InternalAlignment(g2,g3)
    c: InternalAlignment(g4,g3)
    c: InternalAlignment(g5,g3)
    c: Block(g3)
    c: Coincident(g6,g0)
    c: Coincident(g6,g3)
    c: Horizontal(g6)
FEATURE [Part::Extrusion] Extrude014  label="caseScrewPillarBracket002"
  Base = -> Sketch020
  Dir = (0,0,1)
  DirMode = 2
  FaceMakerClass = Part::FaceMakerBullseye
  LengthFwd = 2.4
  LengthRev = 0
  Placement = pos=(13.7,29,13.26) rot=(0,1,0;-1.5708rad)
  Solid = true
  Symmetric = false
